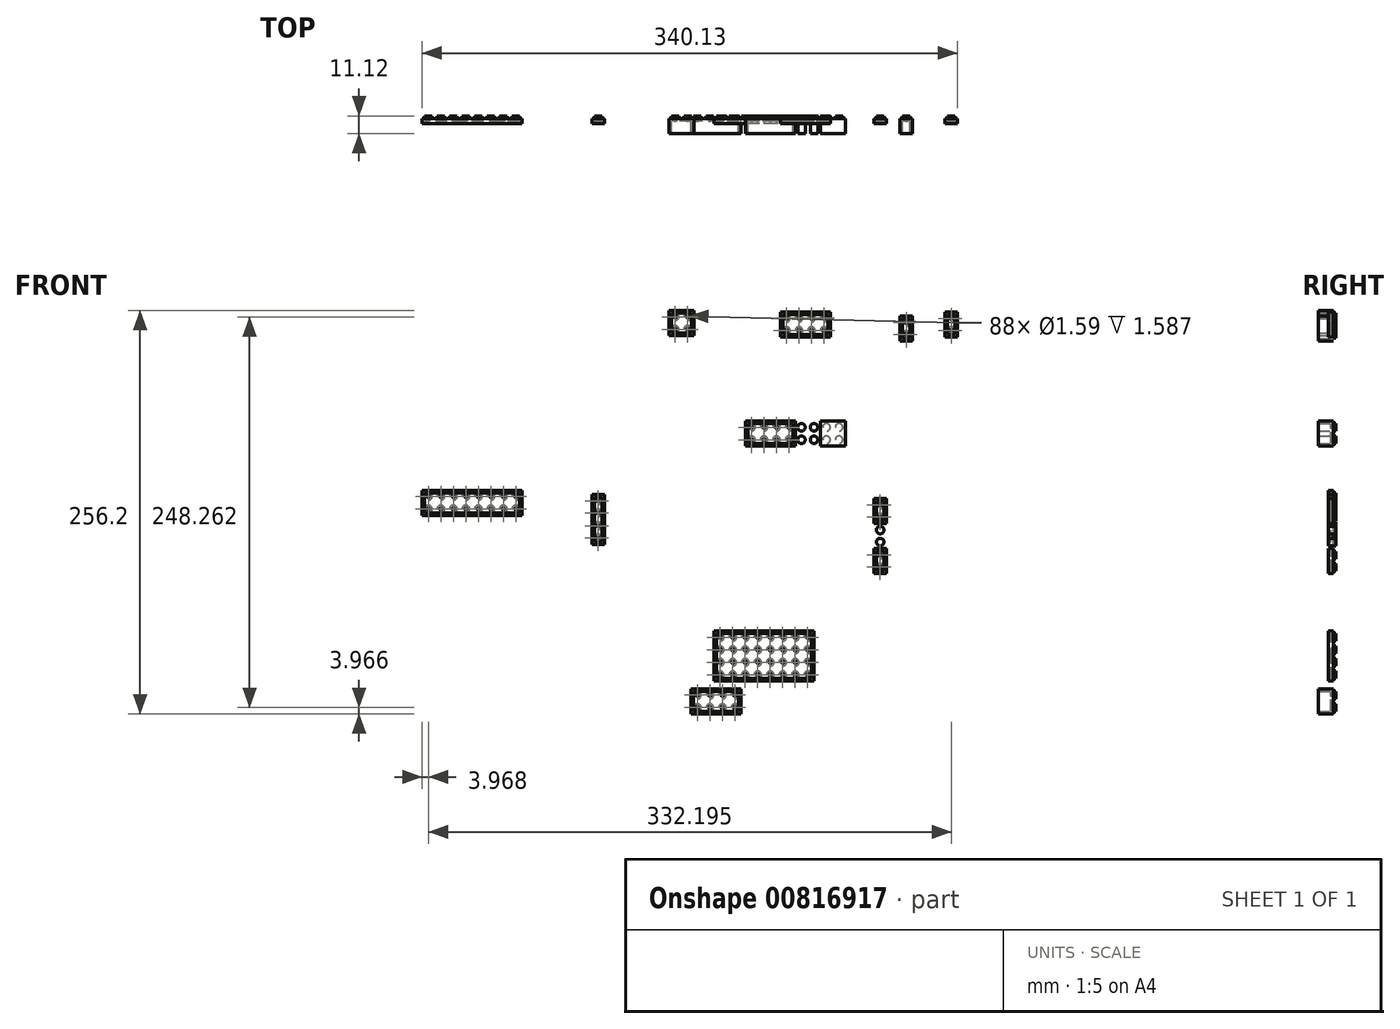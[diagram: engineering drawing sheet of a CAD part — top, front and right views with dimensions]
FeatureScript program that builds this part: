
annotation { "Feature Type Name" : "Feature", "Feature Type Description" : "" }
export const myFeature = defineFeature(function(context is Context, id is Id, definition is map)
    precondition{}
    {
        {
            var Q0;
            Q0=qCreatedBy(makeId("Front.planeOp"),FACE);
            var sketch = newSketch(context, id + "F0", { "sketchPlane" : qUnion([Q0])});
            skLineSegment(sketch, "E0.bottom", {"start": v(-97.11, 110.8) * mm, "end": v(-112.99, 110.8) * mm});
            skLineSegment(sketch, "E0.top", {"start": v(-97.11, 126.67) * mm, "end": v(-112.99, 126.67) * mm});
            skLineSegment(sketch, "E0.left", {"start": v(-97.11, 110.8) * mm, "end": v(-97.11, 126.67) * mm});
            skLineSegment(sketch, "E0.right", {"start": v(-112.99, 110.8) * mm, "end": v(-112.99, 126.67) * mm});
            skPoint(sketch, "E0.middle", {"position": v(-105.05, 118.73) * mm});
            skLineSegment(sketch, "E1", {"start": v(-97.11, 118.73) * mm, "end": v(-112.99, 118.73) * mm, "construction": true});
            skLineSegment(sketch, "E2", {"start": v(-105.05, 126.67) * mm, "end": v(-105.05, 110.8) * mm, "construction": true});
            skLineSegment(sketch, "E3.bottom", {"start": v(-101.08, 114.76) * mm, "end": v(-109.02, 114.76) * mm, "construction": true});
            skLineSegment(sketch, "E3.top", {"start": v(-101.08, 122.7) * mm, "end": v(-109.02, 122.7) * mm, "construction": true});
            skLineSegment(sketch, "E3.left", {"start": v(-101.08, 114.76) * mm, "end": v(-101.08, 122.7) * mm, "construction": true});
            skLineSegment(sketch, "E3.right", {"start": v(-109.02, 114.76) * mm, "end": v(-109.02, 122.7) * mm, "construction": true});
            skCircle(sketch, "E4", {"center": v(-109.02, 122.7) * mm, "radius": 2.38 * mm});
            skCircle(sketch, "E5", {"center": v(-101.08, 122.7) * mm, "radius": 2.38 * mm});
            skCircle(sketch, "E6", {"center": v(-101.08, 114.76) * mm, "radius": 2.38 * mm});
            skCircle(sketch, "E7", {"center": v(-109.02, 114.76) * mm, "radius": 2.38 * mm});
            skLineSegment(sketch, "E8.bottom", {"start": v(-26.35, 109.94) * mm, "end": v(-42.23, 109.94) * mm});
            skLineSegment(sketch, "E8.top", {"start": v(-26.35, 125.82) * mm, "end": v(-42.23, 125.82) * mm});
            skLineSegment(sketch, "E8.left", {"start": v(-26.35, 109.94) * mm, "end": v(-26.35, 125.82) * mm});
            skLineSegment(sketch, "E8.right", {"start": v(-42.23, 109.94) * mm, "end": v(-42.23, 125.82) * mm});
            skPoint(sketch, "E8.middle", {"position": v(-34.29, 117.88) * mm});
            skLineSegment(sketch, "E9", {"start": v(-26.35, 117.88) * mm, "end": v(-42.23, 117.88) * mm, "construction": true});
            skLineSegment(sketch, "E10", {"start": v(-34.29, 125.82) * mm, "end": v(-34.29, 109.94) * mm, "construction": true});
            skLineSegment(sketch, "E11.bottom", {"start": v(-30.32, 113.91) * mm, "end": v(-38.26, 113.91) * mm, "construction": true});
            skLineSegment(sketch, "E11.top", {"start": v(-30.32, 121.85) * mm, "end": v(-38.26, 121.85) * mm, "construction": true});
            skLineSegment(sketch, "E11.left", {"start": v(-30.32, 113.91) * mm, "end": v(-30.32, 121.85) * mm, "construction": true});
            skLineSegment(sketch, "E11.right", {"start": v(-38.26, 113.91) * mm, "end": v(-38.26, 121.85) * mm, "construction": true});
            skCircle(sketch, "E12", {"center": v(-38.26, 121.85) * mm, "radius": 2.38 * mm});
            skCircle(sketch, "E13", {"center": v(-30.32, 121.85) * mm, "radius": 2.38 * mm});
            skCircle(sketch, "E14", {"center": v(-30.32, 113.91) * mm, "radius": 2.38 * mm});
            skCircle(sketch, "E15", {"center": v(-38.26, 113.91) * mm, "radius": 2.38 * mm});
            skLineSegment(sketch, "E16.bottom", {"start": v(-10.48, 109.94) * mm, "end": v(-26.35, 109.94) * mm});
            skLineSegment(sketch, "E16.top", {"start": v(-10.48, 125.82) * mm, "end": v(-26.35, 125.82) * mm});
            skLineSegment(sketch, "E16.left", {"start": v(-10.48, 109.94) * mm, "end": v(-10.48, 125.82) * mm});
            skPoint(sketch, "E16.middle", {"position": v(-18.41, 117.88) * mm});
            skLineSegment(sketch, "E17", {"start": v(-10.48, 117.88) * mm, "end": v(-26.35, 117.88) * mm, "construction": true});
            skLineSegment(sketch, "E18", {"start": v(-18.41, 125.82) * mm, "end": v(-18.41, 109.94) * mm, "construction": true});
            skLineSegment(sketch, "E19.bottom", {"start": v(-14.44, 113.91) * mm, "end": v(-22.38, 113.91) * mm, "construction": true});
            skLineSegment(sketch, "E19.top", {"start": v(-14.44, 121.85) * mm, "end": v(-22.38, 121.85) * mm, "construction": true});
            skLineSegment(sketch, "E19.left", {"start": v(-14.44, 113.91) * mm, "end": v(-14.44, 121.85) * mm, "construction": true});
            skLineSegment(sketch, "E19.right", {"start": v(-22.38, 113.91) * mm, "end": v(-22.38, 121.85) * mm, "construction": true});
            skCircle(sketch, "E20", {"center": v(-22.38, 121.85) * mm, "radius": 2.38 * mm});
            skCircle(sketch, "E21", {"center": v(-14.44, 121.85) * mm, "radius": 2.38 * mm});
            skCircle(sketch, "E22", {"center": v(-14.44, 113.91) * mm, "radius": 2.38 * mm});
            skCircle(sketch, "E23", {"center": v(-22.38, 113.91) * mm, "radius": 2.38 * mm});
            skLineSegment(sketch, "E24.bottom", {"start": v(41.77, 107.4) * mm, "end": v(33.85, 107.4) * mm});
            skLineSegment(sketch, "E24.top", {"start": v(41.77, 123.28) * mm, "end": v(33.85, 123.28) * mm});
            skLineSegment(sketch, "E24.left", {"start": v(41.77, 107.4) * mm, "end": v(41.77, 123.28) * mm});
            skLineSegment(sketch, "E24.right", {"start": v(33.85, 107.4) * mm, "end": v(33.85, 123.28) * mm});
            skPoint(sketch, "E24.middle", {"position": v(37.8, 115.34) * mm});
            skLineSegment(sketch, "E25", {"start": v(37.8, 123.28) * mm, "end": v(37.8, 107.4) * mm, "construction": true});
            skLineSegment(sketch, "E26", {"start": v(33.85, 115.34) * mm, "end": v(41.77, 115.34) * mm, "construction": true});
            skLineSegment(sketch, "E27", {"start": v(33.85, 111.53) * mm, "end": v(41.77, 111.53) * mm, "construction": true});
            skLineSegment(sketch, "E28", {"start": v(33.85, 119.14) * mm, "end": v(41.77, 119.14) * mm, "construction": true});
            skCircle(sketch, "E29", {"center": v(37.8, 119.14) * mm, "radius": 2.38 * mm});
            skCircle(sketch, "E30", {"center": v(37.8, 111.53) * mm, "radius": 2.38 * mm});
            skLineSegment(sketch, "E31.bottom", {"start": v(-68.44, -92.83) * mm, "end": v(-84.32, -92.83) * mm});
            skLineSegment(sketch, "E31.top", {"start": v(-68.44, -76.96) * mm, "end": v(-84.32, -76.96) * mm});
            skLineSegment(sketch, "E31.left", {"start": v(-68.44, -92.83) * mm, "end": v(-68.44, -76.96) * mm});
            skLineSegment(sketch, "E31.right", {"start": v(-84.32, -92.83) * mm, "end": v(-84.32, -76.96) * mm});
            skPoint(sketch, "E31.middle", {"position": v(-76.38, -84.9) * mm});
            skLineSegment(sketch, "E32", {"start": v(-68.44, -84.9) * mm, "end": v(-84.32, -84.9) * mm, "construction": true});
            skLineSegment(sketch, "E33", {"start": v(-76.38, -76.96) * mm, "end": v(-76.38, -92.83) * mm, "construction": true});
            skLineSegment(sketch, "E34.bottom", {"start": v(-72.4, -88.86) * mm, "end": v(-80.35, -88.86) * mm, "construction": true});
            skLineSegment(sketch, "E34.top", {"start": v(-72.4, -80.93) * mm, "end": v(-80.35, -80.93) * mm, "construction": true});
            skLineSegment(sketch, "E34.left", {"start": v(-72.4, -88.86) * mm, "end": v(-72.4, -80.93) * mm, "construction": true});
            skLineSegment(sketch, "E34.right", {"start": v(-80.35, -88.86) * mm, "end": v(-80.35, -80.93) * mm, "construction": true});
            skCircle(sketch, "E35", {"center": v(-80.35, -80.93) * mm, "radius": 2.38 * mm});
            skCircle(sketch, "E36", {"center": v(-72.4, -80.93) * mm, "radius": 2.38 * mm});
            skCircle(sketch, "E37", {"center": v(-72.4, -88.86) * mm, "radius": 2.38 * mm});
            skCircle(sketch, "E38", {"center": v(-80.35, -88.86) * mm, "radius": 2.38 * mm});
            skLineSegment(sketch, "E39.bottom", {"start": v(-48.58, 40.58) * mm, "end": v(-64.45, 40.58) * mm});
            skLineSegment(sketch, "E39.top", {"start": v(-48.58, 56.46) * mm, "end": v(-64.45, 56.46) * mm});
            skLineSegment(sketch, "E39.left", {"start": v(-48.58, 40.58) * mm, "end": v(-48.58, 56.46) * mm});
            skLineSegment(sketch, "E39.right", {"start": v(-64.45, 40.58) * mm, "end": v(-64.45, 56.46) * mm});
            skPoint(sketch, "E39.middle", {"position": v(-56.51, 48.52) * mm});
            skLineSegment(sketch, "E40", {"start": v(-48.58, 48.52) * mm, "end": v(-64.45, 48.52) * mm, "construction": true});
            skLineSegment(sketch, "E41", {"start": v(-56.51, 56.46) * mm, "end": v(-56.51, 40.58) * mm, "construction": true});
            skLineSegment(sketch, "E42.bottom", {"start": v(-52.54, 44.55) * mm, "end": v(-60.48, 44.55) * mm, "construction": true});
            skLineSegment(sketch, "E42.top", {"start": v(-52.54, 52.49) * mm, "end": v(-60.48, 52.49) * mm, "construction": true});
            skLineSegment(sketch, "E42.left", {"start": v(-52.54, 44.55) * mm, "end": v(-52.54, 52.49) * mm, "construction": true});
            skLineSegment(sketch, "E42.right", {"start": v(-60.48, 44.55) * mm, "end": v(-60.48, 52.49) * mm, "construction": true});
            skCircle(sketch, "E43", {"center": v(-60.48, 52.49) * mm, "radius": 2.38 * mm});
            skCircle(sketch, "E44", {"center": v(-52.54, 52.49) * mm, "radius": 2.38 * mm});
            skCircle(sketch, "E45", {"center": v(-52.54, 44.55) * mm, "radius": 2.38 * mm});
            skCircle(sketch, "E46", {"center": v(-60.48, 44.55) * mm, "radius": 2.38 * mm});
            skLineSegment(sketch, "E47.bottom", {"start": v(-32.7, 40.58) * mm, "end": v(-48.58, 40.58) * mm});
            skLineSegment(sketch, "E47.top", {"start": v(-32.7, 56.46) * mm, "end": v(-48.58, 56.46) * mm});
            skLineSegment(sketch, "E47.left", {"start": v(-32.7, 40.58) * mm, "end": v(-32.7, 56.46) * mm});
            skPoint(sketch, "E47.middle", {"position": v(-40.64, 48.52) * mm});
            skLineSegment(sketch, "E48", {"start": v(-32.7, 48.52) * mm, "end": v(-48.58, 48.52) * mm, "construction": true});
            skLineSegment(sketch, "E49", {"start": v(-40.64, 56.46) * mm, "end": v(-40.64, 40.58) * mm, "construction": true});
            skLineSegment(sketch, "E50.bottom", {"start": v(-36.67, 44.55) * mm, "end": v(-44.6, 44.55) * mm, "construction": true});
            skLineSegment(sketch, "E50.top", {"start": v(-36.67, 52.49) * mm, "end": v(-44.6, 52.49) * mm, "construction": true});
            skLineSegment(sketch, "E50.left", {"start": v(-36.67, 44.55) * mm, "end": v(-36.67, 52.49) * mm, "construction": true});
            skLineSegment(sketch, "E50.right", {"start": v(-44.6, 44.55) * mm, "end": v(-44.6, 52.49) * mm, "construction": true});
            skCircle(sketch, "E51", {"center": v(-44.6, 52.49) * mm, "radius": 2.38 * mm});
            skCircle(sketch, "E52", {"center": v(-36.67, 52.49) * mm, "radius": 2.38 * mm});
            skCircle(sketch, "E53", {"center": v(-36.67, 44.55) * mm, "radius": 2.38 * mm});
            skCircle(sketch, "E54", {"center": v(-44.6, 44.55) * mm, "radius": 2.38 * mm});
            skLineSegment(sketch, "E55.bottom", {"start": v(70.44, 109.95) * mm, "end": v(62.51, 109.95) * mm});
            skLineSegment(sketch, "E55.top", {"start": v(70.44, 125.83) * mm, "end": v(62.51, 125.83) * mm});
            skLineSegment(sketch, "E55.left", {"start": v(70.44, 109.95) * mm, "end": v(70.44, 125.83) * mm});
            skLineSegment(sketch, "E55.right", {"start": v(62.51, 109.95) * mm, "end": v(62.51, 125.83) * mm});
            skPoint(sketch, "E55.middle", {"position": v(66.47, 117.89) * mm});
            skLineSegment(sketch, "E56", {"start": v(66.47, 125.83) * mm, "end": v(66.47, 109.95) * mm, "construction": true});
            skLineSegment(sketch, "E57", {"start": v(62.51, 117.89) * mm, "end": v(70.44, 117.89) * mm, "construction": true});
            skLineSegment(sketch, "E58", {"start": v(62.51, 114.08) * mm, "end": v(70.44, 114.08) * mm, "construction": true});
            skLineSegment(sketch, "E59", {"start": v(62.51, 121.69) * mm, "end": v(70.44, 121.69) * mm, "construction": true});
            skCircle(sketch, "E60", {"center": v(66.47, 121.69) * mm, "radius": 2.38 * mm});
            skCircle(sketch, "E61", {"center": v(66.47, 114.08) * mm, "radius": 2.38 * mm});
            skLineSegment(sketch, "E62.bottom", {"start": v(-52.57, -92.83) * mm, "end": v(-68.44, -92.83) * mm});
            skLineSegment(sketch, "E62.top", {"start": v(-52.57, -76.96) * mm, "end": v(-68.44, -76.96) * mm});
            skLineSegment(sketch, "E62.left", {"start": v(-52.57, -92.83) * mm, "end": v(-52.57, -76.96) * mm});
            skPoint(sketch, "E62.middle", {"position": v(-60.5, -84.9) * mm});
            skLineSegment(sketch, "E63", {"start": v(-52.57, -84.9) * mm, "end": v(-68.44, -84.9) * mm, "construction": true});
            skLineSegment(sketch, "E64", {"start": v(-60.5, -76.96) * mm, "end": v(-60.5, -92.83) * mm, "construction": true});
            skLineSegment(sketch, "E65.bottom", {"start": v(-56.53, -88.86) * mm, "end": v(-64.47, -88.86) * mm, "construction": true});
            skLineSegment(sketch, "E65.top", {"start": v(-56.53, -80.93) * mm, "end": v(-64.47, -80.93) * mm, "construction": true});
            skLineSegment(sketch, "E65.left", {"start": v(-56.53, -88.86) * mm, "end": v(-56.53, -80.93) * mm, "construction": true});
            skLineSegment(sketch, "E65.right", {"start": v(-64.47, -88.86) * mm, "end": v(-64.47, -80.93) * mm, "construction": true});
            skCircle(sketch, "E66", {"center": v(-64.47, -80.93) * mm, "radius": 2.38 * mm});
            skCircle(sketch, "E67", {"center": v(-56.53, -80.93) * mm, "radius": 2.38 * mm});
            skCircle(sketch, "E68", {"center": v(-56.53, -88.86) * mm, "radius": 2.38 * mm});
            skCircle(sketch, "E69", {"center": v(-64.47, -88.86) * mm, "radius": 2.38 * mm});
            skLineSegment(sketch, "E70.bottom", {"start": v(-36.7, -92.83) * mm, "end": v(-52.57, -92.83) * mm});
            skLineSegment(sketch, "E70.top", {"start": v(-36.7, -76.96) * mm, "end": v(-52.57, -76.96) * mm});
            skLineSegment(sketch, "E70.left", {"start": v(-36.7, -92.83) * mm, "end": v(-36.7, -76.96) * mm});
            skPoint(sketch, "E70.middle", {"position": v(-44.63, -84.9) * mm});
            skLineSegment(sketch, "E71", {"start": v(-36.7, -84.9) * mm, "end": v(-52.57, -84.9) * mm, "construction": true});
            skLineSegment(sketch, "E72", {"start": v(-44.63, -76.96) * mm, "end": v(-44.63, -92.83) * mm, "construction": true});
            skLineSegment(sketch, "E73.bottom", {"start": v(-40.66, -88.86) * mm, "end": v(-48.6, -88.86) * mm, "construction": true});
            skLineSegment(sketch, "E73.top", {"start": v(-40.66, -80.93) * mm, "end": v(-48.6, -80.93) * mm, "construction": true});
            skLineSegment(sketch, "E73.left", {"start": v(-40.66, -88.86) * mm, "end": v(-40.66, -80.93) * mm, "construction": true});
            skLineSegment(sketch, "E73.right", {"start": v(-48.6, -88.86) * mm, "end": v(-48.6, -80.93) * mm, "construction": true});
            skCircle(sketch, "E74", {"center": v(-48.6, -80.93) * mm, "radius": 2.38 * mm});
            skCircle(sketch, "E75", {"center": v(-40.66, -80.93) * mm, "radius": 2.38 * mm});
            skCircle(sketch, "E76", {"center": v(-40.66, -88.86) * mm, "radius": 2.38 * mm});
            skCircle(sketch, "E77", {"center": v(-48.6, -88.86) * mm, "radius": 2.38 * mm});
            skLineSegment(sketch, "E78.bottom", {"start": v(-20.82, -92.83) * mm, "end": v(-36.7, -92.83) * mm});
            skLineSegment(sketch, "E78.top", {"start": v(-20.82, -76.96) * mm, "end": v(-36.7, -76.96) * mm});
            skLineSegment(sketch, "E78.left", {"start": v(-20.82, -92.83) * mm, "end": v(-20.82, -76.96) * mm});
            skPoint(sketch, "E78.middle", {"position": v(-28.75, -84.9) * mm});
            skLineSegment(sketch, "E79", {"start": v(-20.82, -84.9) * mm, "end": v(-36.7, -84.9) * mm, "construction": true});
            skLineSegment(sketch, "E80", {"start": v(-28.75, -76.96) * mm, "end": v(-28.75, -92.83) * mm, "construction": true});
            skLineSegment(sketch, "E81.bottom", {"start": v(-24.78, -88.86) * mm, "end": v(-32.72, -88.86) * mm, "construction": true});
            skLineSegment(sketch, "E81.top", {"start": v(-24.78, -80.93) * mm, "end": v(-32.72, -80.93) * mm, "construction": true});
            skLineSegment(sketch, "E81.left", {"start": v(-24.78, -88.86) * mm, "end": v(-24.78, -80.93) * mm, "construction": true});
            skLineSegment(sketch, "E81.right", {"start": v(-32.72, -88.86) * mm, "end": v(-32.72, -80.93) * mm, "construction": true});
            skCircle(sketch, "E82", {"center": v(-32.72, -80.93) * mm, "radius": 2.38 * mm});
            skCircle(sketch, "E83", {"center": v(-24.78, -80.93) * mm, "radius": 2.38 * mm});
            skCircle(sketch, "E84", {"center": v(-24.78, -88.86) * mm, "radius": 2.38 * mm});
            skCircle(sketch, "E85", {"center": v(-32.72, -88.86) * mm, "radius": 2.38 * mm});
            skLineSegment(sketch, "E86.bottom", {"start": v(25.2, -8.63) * mm, "end": v(17.27, -8.63) * mm});
            skLineSegment(sketch, "E86.top", {"start": v(25.2, 7.25) * mm, "end": v(17.27, 7.25) * mm});
            skLineSegment(sketch, "E86.left", {"start": v(25.2, -8.63) * mm, "end": v(25.2, 7.25) * mm});
            skLineSegment(sketch, "E86.right", {"start": v(17.27, -8.63) * mm, "end": v(17.27, 7.25) * mm});
            skPoint(sketch, "E86.middle", {"position": v(21.23, -0.69) * mm});
            skLineSegment(sketch, "E87", {"start": v(21.23, 7.25) * mm, "end": v(21.23, -8.63) * mm, "construction": true});
            skLineSegment(sketch, "E88", {"start": v(17.27, -0.69) * mm, "end": v(25.2, -0.69) * mm, "construction": true});
            skLineSegment(sketch, "E89", {"start": v(17.27, -4.5) * mm, "end": v(25.2, -4.5) * mm, "construction": true});
            skLineSegment(sketch, "E90", {"start": v(17.27, 3.1) * mm, "end": v(25.2, 3.1) * mm, "construction": true});
            skCircle(sketch, "E91", {"center": v(21.23, 3.1) * mm, "radius": 2.38 * mm});
            skCircle(sketch, "E92", {"center": v(21.23, -4.5) * mm, "radius": 2.38 * mm});
            skLineSegment(sketch, "E93.bottom", {"start": v(-68.44, -108.7) * mm, "end": v(-84.32, -108.7) * mm});
            skLineSegment(sketch, "E93.left", {"start": v(-68.44, -108.7) * mm, "end": v(-68.44, -92.83) * mm});
            skLineSegment(sketch, "E93.right", {"start": v(-84.32, -108.7) * mm, "end": v(-84.32, -92.83) * mm});
            skPoint(sketch, "E93.middle", {"position": v(-76.38, -100.77) * mm});
            skLineSegment(sketch, "E94", {"start": v(-68.44, -100.77) * mm, "end": v(-84.32, -100.77) * mm, "construction": true});
            skLineSegment(sketch, "E95", {"start": v(-76.38, -92.83) * mm, "end": v(-76.38, -108.7) * mm, "construction": true});
            skLineSegment(sketch, "E96.bottom", {"start": v(-72.4, -104.74) * mm, "end": v(-80.35, -104.74) * mm, "construction": true});
            skLineSegment(sketch, "E96.top", {"start": v(-72.4, -96.8) * mm, "end": v(-80.35, -96.8) * mm, "construction": true});
            skLineSegment(sketch, "E96.left", {"start": v(-72.4, -104.74) * mm, "end": v(-72.4, -96.8) * mm, "construction": true});
            skLineSegment(sketch, "E96.right", {"start": v(-80.35, -104.74) * mm, "end": v(-80.35, -96.8) * mm, "construction": true});
            skCircle(sketch, "E97", {"center": v(-80.35, -96.8) * mm, "radius": 2.38 * mm});
            skCircle(sketch, "E98", {"center": v(-72.4, -96.8) * mm, "radius": 2.38 * mm});
            skCircle(sketch, "E99", {"center": v(-72.4, -104.74) * mm, "radius": 2.38 * mm});
            skCircle(sketch, "E100", {"center": v(-80.35, -104.74) * mm, "radius": 2.38 * mm});
            skLineSegment(sketch, "E101.bottom", {"start": v(-82.95, -129.53) * mm, "end": v(-98.82, -129.53) * mm});
            skLineSegment(sketch, "E101.top", {"start": v(-82.95, -113.66) * mm, "end": v(-98.82, -113.66) * mm});
            skLineSegment(sketch, "E101.left", {"start": v(-82.95, -129.53) * mm, "end": v(-82.95, -113.66) * mm});
            skLineSegment(sketch, "E101.right", {"start": v(-98.82, -129.53) * mm, "end": v(-98.82, -113.66) * mm});
            skPoint(sketch, "E101.middle", {"position": v(-90.89, -121.6) * mm});
            skLineSegment(sketch, "E102", {"start": v(-82.95, -121.6) * mm, "end": v(-98.82, -121.6) * mm, "construction": true});
            skLineSegment(sketch, "E103", {"start": v(-90.89, -113.66) * mm, "end": v(-90.89, -129.53) * mm, "construction": true});
            skLineSegment(sketch, "E104.bottom", {"start": v(-86.92, -125.56) * mm, "end": v(-94.85, -125.56) * mm, "construction": true});
            skLineSegment(sketch, "E104.top", {"start": v(-86.92, -117.63) * mm, "end": v(-94.85, -117.63) * mm, "construction": true});
            skLineSegment(sketch, "E104.left", {"start": v(-86.92, -125.56) * mm, "end": v(-86.92, -117.63) * mm, "construction": true});
            skLineSegment(sketch, "E104.right", {"start": v(-94.85, -125.56) * mm, "end": v(-94.85, -117.63) * mm, "construction": true});
            skCircle(sketch, "E105", {"center": v(-94.85, -117.63) * mm, "radius": 2.38 * mm});
            skCircle(sketch, "E106", {"center": v(-86.92, -117.63) * mm, "radius": 2.38 * mm});
            skCircle(sketch, "E107", {"center": v(-86.92, -125.56) * mm, "radius": 2.38 * mm});
            skCircle(sketch, "E108", {"center": v(-94.85, -125.56) * mm, "radius": 2.38 * mm});
            skLineSegment(sketch, "E109.bottom", {"start": v(-67.07, -129.53) * mm, "end": v(-82.95, -129.53) * mm});
            skLineSegment(sketch, "E109.top", {"start": v(-67.07, -113.66) * mm, "end": v(-82.95, -113.66) * mm});
            skLineSegment(sketch, "E109.left", {"start": v(-67.07, -129.53) * mm, "end": v(-67.07, -113.66) * mm});
            skPoint(sketch, "E109.middle", {"position": v(-75.01, -121.6) * mm});
            skLineSegment(sketch, "E110", {"start": v(-67.07, -121.6) * mm, "end": v(-82.95, -121.6) * mm, "construction": true});
            skLineSegment(sketch, "E111", {"start": v(-75.01, -113.66) * mm, "end": v(-75.01, -129.53) * mm, "construction": true});
            skLineSegment(sketch, "E112.bottom", {"start": v(-71.04, -125.56) * mm, "end": v(-78.98, -125.56) * mm, "construction": true});
            skLineSegment(sketch, "E112.top", {"start": v(-71.04, -117.63) * mm, "end": v(-78.98, -117.63) * mm, "construction": true});
            skLineSegment(sketch, "E112.left", {"start": v(-71.04, -125.56) * mm, "end": v(-71.04, -117.63) * mm, "construction": true});
            skLineSegment(sketch, "E112.right", {"start": v(-78.98, -125.56) * mm, "end": v(-78.98, -117.63) * mm, "construction": true});
            skCircle(sketch, "E113", {"center": v(-78.98, -117.63) * mm, "radius": 2.38 * mm});
            skCircle(sketch, "E114", {"center": v(-71.04, -117.63) * mm, "radius": 2.38 * mm});
            skCircle(sketch, "E115", {"center": v(-71.04, -125.56) * mm, "radius": 2.38 * mm});
            skCircle(sketch, "E116", {"center": v(-78.98, -125.56) * mm, "radius": 2.38 * mm});
            skLineSegment(sketch, "E117.bottom", {"start": v(25.2, -40.38) * mm, "end": v(17.27, -40.38) * mm});
            skLineSegment(sketch, "E117.top", {"start": v(25.2, -24.5) * mm, "end": v(17.27, -24.5) * mm});
            skLineSegment(sketch, "E117.left", {"start": v(25.2, -40.38) * mm, "end": v(25.2, -24.5) * mm});
            skLineSegment(sketch, "E117.right", {"start": v(17.27, -40.38) * mm, "end": v(17.27, -24.5) * mm});
            skPoint(sketch, "E117.middle", {"position": v(21.23, -32.44) * mm});
            skLineSegment(sketch, "E118", {"start": v(21.23, -24.5) * mm, "end": v(21.23, -40.38) * mm, "construction": true});
            skLineSegment(sketch, "E119", {"start": v(17.27, -32.44) * mm, "end": v(25.2, -32.44) * mm, "construction": true});
            skLineSegment(sketch, "E120", {"start": v(17.27, -36.25) * mm, "end": v(25.2, -36.25) * mm, "construction": true});
            skLineSegment(sketch, "E121", {"start": v(17.27, -28.64) * mm, "end": v(25.2, -28.64) * mm, "construction": true});
            skCircle(sketch, "E122", {"center": v(21.23, -28.64) * mm, "radius": 2.38 * mm});
            skCircle(sketch, "E123", {"center": v(21.23, -36.25) * mm, "radius": 2.38 * mm});
            skLineSegment(sketch, "E124.bottom", {"start": v(-52.57, -108.7) * mm, "end": v(-68.44, -108.7) * mm});
            skLineSegment(sketch, "E124.left", {"start": v(-52.57, -108.7) * mm, "end": v(-52.57, -92.83) * mm});
            skPoint(sketch, "E124.middle", {"position": v(-60.5, -100.77) * mm});
            skLineSegment(sketch, "E125", {"start": v(-52.57, -100.77) * mm, "end": v(-68.44, -100.77) * mm, "construction": true});
            skLineSegment(sketch, "E126", {"start": v(-60.5, -92.83) * mm, "end": v(-60.5, -108.7) * mm, "construction": true});
            skLineSegment(sketch, "E127.bottom", {"start": v(-56.53, -104.74) * mm, "end": v(-64.47, -104.74) * mm, "construction": true});
            skLineSegment(sketch, "E127.top", {"start": v(-56.53, -96.8) * mm, "end": v(-64.47, -96.8) * mm, "construction": true});
            skLineSegment(sketch, "E127.left", {"start": v(-56.53, -104.74) * mm, "end": v(-56.53, -96.8) * mm, "construction": true});
            skLineSegment(sketch, "E127.right", {"start": v(-64.47, -104.74) * mm, "end": v(-64.47, -96.8) * mm, "construction": true});
            skCircle(sketch, "E128", {"center": v(-64.47, -96.8) * mm, "radius": 2.38 * mm});
            skCircle(sketch, "E129", {"center": v(-56.53, -96.8) * mm, "radius": 2.38 * mm});
            skCircle(sketch, "E130", {"center": v(-56.53, -104.74) * mm, "radius": 2.38 * mm});
            skCircle(sketch, "E131", {"center": v(-64.47, -104.74) * mm, "radius": 2.38 * mm});
            skLineSegment(sketch, "E132.bottom", {"start": v(-36.7, -108.7) * mm, "end": v(-52.57, -108.7) * mm});
            skLineSegment(sketch, "E132.left", {"start": v(-36.7, -108.7) * mm, "end": v(-36.7, -92.83) * mm});
            skPoint(sketch, "E132.middle", {"position": v(-44.63, -100.77) * mm});
            skLineSegment(sketch, "E133", {"start": v(-36.7, -100.77) * mm, "end": v(-52.57, -100.77) * mm, "construction": true});
            skLineSegment(sketch, "E134", {"start": v(-44.63, -92.83) * mm, "end": v(-44.63, -108.7) * mm, "construction": true});
            skLineSegment(sketch, "E135.bottom", {"start": v(-40.66, -104.74) * mm, "end": v(-48.6, -104.74) * mm, "construction": true});
            skLineSegment(sketch, "E135.top", {"start": v(-40.66, -96.8) * mm, "end": v(-48.6, -96.8) * mm, "construction": true});
            skLineSegment(sketch, "E135.left", {"start": v(-40.66, -104.74) * mm, "end": v(-40.66, -96.8) * mm, "construction": true});
            skLineSegment(sketch, "E135.right", {"start": v(-48.6, -104.74) * mm, "end": v(-48.6, -96.8) * mm, "construction": true});
            skCircle(sketch, "E136", {"center": v(-48.6, -96.8) * mm, "radius": 2.38 * mm});
            skCircle(sketch, "E137", {"center": v(-40.66, -96.8) * mm, "radius": 2.38 * mm});
            skCircle(sketch, "E138", {"center": v(-40.66, -104.74) * mm, "radius": 2.38 * mm});
            skCircle(sketch, "E139", {"center": v(-48.6, -104.74) * mm, "radius": 2.38 * mm});
            skLineSegment(sketch, "E140.bottom", {"start": v(-20.82, -108.7) * mm, "end": v(-36.7, -108.7) * mm});
            skLineSegment(sketch, "E140.left", {"start": v(-20.82, -108.7) * mm, "end": v(-20.82, -92.83) * mm});
            skPoint(sketch, "E140.middle", {"position": v(-28.75, -100.77) * mm});
            skLineSegment(sketch, "E141", {"start": v(-20.82, -100.77) * mm, "end": v(-36.7, -100.77) * mm, "construction": true});
            skLineSegment(sketch, "E142", {"start": v(-28.75, -92.83) * mm, "end": v(-28.75, -108.7) * mm, "construction": true});
            skLineSegment(sketch, "E143.bottom", {"start": v(-24.78, -104.74) * mm, "end": v(-32.72, -104.74) * mm, "construction": true});
            skLineSegment(sketch, "E143.top", {"start": v(-24.78, -96.8) * mm, "end": v(-32.72, -96.8) * mm, "construction": true});
            skLineSegment(sketch, "E143.left", {"start": v(-24.78, -104.74) * mm, "end": v(-24.78, -96.8) * mm, "construction": true});
            skLineSegment(sketch, "E143.right", {"start": v(-32.72, -104.74) * mm, "end": v(-32.72, -96.8) * mm, "construction": true});
            skCircle(sketch, "E144", {"center": v(-32.72, -96.8) * mm, "radius": 2.38 * mm});
            skCircle(sketch, "E145", {"center": v(-24.78, -96.8) * mm, "radius": 2.38 * mm});
            skCircle(sketch, "E146", {"center": v(-24.78, -104.74) * mm, "radius": 2.38 * mm});
            skCircle(sketch, "E147", {"center": v(-32.72, -104.74) * mm, "radius": 2.38 * mm});
            skLineSegment(sketch, "E148.left", {"start": v(25.2, -24.5) * mm, "end": v(25.2, -8.63) * mm});
            skLineSegment(sketch, "E148.right", {"start": v(17.27, -24.5) * mm, "end": v(17.27, -8.63) * mm});
            skPoint(sketch, "E148.middle", {"position": v(21.23, -16.56) * mm});
            skLineSegment(sketch, "E149", {"start": v(21.23, -8.63) * mm, "end": v(21.23, -24.5) * mm, "construction": true});
            skLineSegment(sketch, "E150", {"start": v(17.27, -16.56) * mm, "end": v(25.2, -16.56) * mm, "construction": true});
            skLineSegment(sketch, "E151", {"start": v(17.27, -20.37) * mm, "end": v(25.2, -20.37) * mm, "construction": true});
            skLineSegment(sketch, "E152", {"start": v(17.27, -12.77) * mm, "end": v(25.2, -12.77) * mm, "construction": true});
            skCircle(sketch, "E153", {"center": v(21.23, -12.77) * mm, "radius": 2.38 * mm});
            skCircle(sketch, "E154", {"center": v(21.23, -20.37) * mm, "radius": 2.38 * mm});
            skLineSegment(sketch, "E155.bottom", {"start": v(-32.7, 40.58) * mm, "end": v(-0.95, 40.58) * mm});
            skLineSegment(sketch, "E155.top", {"start": v(-32.7, 56.46) * mm, "end": v(-0.95, 56.46) * mm});
            skLineSegment(sketch, "E155.right", {"start": v(-0.95, 40.58) * mm, "end": v(-0.95, 56.46) * mm});
            skLineSegment(sketch, "E156", {"start": v(-16.83, 56.46) * mm, "end": v(-16.83, 40.58) * mm});
            skLineSegment(sketch, "E157", {"start": v(-32.7, 48.52) * mm, "end": v(-0.95, 48.52) * mm, "construction": true});
            skLineSegment(sketch, "E158", {"start": v(-24.76, 40.58) * mm, "end": v(-24.76, 56.46) * mm, "construction": true});
            skLineSegment(sketch, "E159", {"start": v(-8.89, 40.58) * mm, "end": v(-8.89, 56.46) * mm, "construction": true});
            skLineSegment(sketch, "E160.bottom", {"start": v(-20.8, 44.55) * mm, "end": v(-28.73, 44.55) * mm, "construction": true});
            skLineSegment(sketch, "E160.top", {"start": v(-20.8, 52.49) * mm, "end": v(-28.73, 52.49) * mm, "construction": true});
            skLineSegment(sketch, "E160.left", {"start": v(-20.8, 44.55) * mm, "end": v(-20.8, 52.49) * mm, "construction": true});
            skLineSegment(sketch, "E160.right", {"start": v(-28.73, 44.55) * mm, "end": v(-28.73, 52.49) * mm, "construction": true});
            skPoint(sketch, "E160.middle", {"position": v(-24.76, 48.52) * mm});
            skLineSegment(sketch, "E161.bottom", {"start": v(-12.86, 44.55) * mm, "end": v(-4.92, 44.55) * mm, "construction": true});
            skLineSegment(sketch, "E161.top", {"start": v(-12.86, 52.49) * mm, "end": v(-4.92, 52.49) * mm, "construction": true});
            skLineSegment(sketch, "E161.left", {"start": v(-12.86, 44.55) * mm, "end": v(-12.86, 52.49) * mm, "construction": true});
            skLineSegment(sketch, "E161.right", {"start": v(-4.92, 44.55) * mm, "end": v(-4.92, 52.49) * mm, "construction": true});
            skPoint(sketch, "E161.middle", {"position": v(-8.89, 48.52) * mm});
            skCircle(sketch, "E162", {"center": v(-28.73, 52.49) * mm, "radius": 2.38 * mm});
            skCircle(sketch, "E163", {"center": v(-20.8, 52.49) * mm, "radius": 2.38 * mm});
            skCircle(sketch, "E164", {"center": v(-20.8, 44.55) * mm, "radius": 2.38 * mm});
            skCircle(sketch, "E165", {"center": v(-28.73, 44.55) * mm, "radius": 2.38 * mm});
            skCircle(sketch, "E166", {"center": v(-12.86, 44.55) * mm, "radius": 2.38 * mm});
            skCircle(sketch, "E167", {"center": v(-4.92, 44.55) * mm, "radius": 2.38 * mm});
            skCircle(sketch, "E168", {"center": v(-4.92, 52.49) * mm, "radius": 2.38 * mm});
            skCircle(sketch, "E169", {"center": v(-12.86, 52.49) * mm, "radius": 2.38 * mm});
            skLineSegment(sketch, "E170.bottom", {"start": v(-330.16, -43.54) * mm, "end": v(-346.04, -43.54) * mm});
            skLineSegment(sketch, "E170.top", {"start": v(-330.16, -27.67) * mm, "end": v(-346.04, -27.67) * mm});
            skLineSegment(sketch, "E170.left", {"start": v(-330.16, -43.54) * mm, "end": v(-330.16, -27.67) * mm});
            skLineSegment(sketch, "E170.right", {"start": v(-346.04, -43.54) * mm, "end": v(-346.04, -27.67) * mm});
            skPoint(sketch, "E170.middle", {"position": v(-338.1, -35.6) * mm});
            skLineSegment(sketch, "E171", {"start": v(-330.16, -35.6) * mm, "end": v(-346.04, -35.6) * mm, "construction": true});
            skLineSegment(sketch, "E172", {"start": v(-338.1, -27.67) * mm, "end": v(-338.1, -43.54) * mm, "construction": true});
            skLineSegment(sketch, "E173.bottom", {"start": v(-334.13, -39.57) * mm, "end": v(-342.07, -39.57) * mm, "construction": true});
            skLineSegment(sketch, "E173.top", {"start": v(-334.13, -31.63) * mm, "end": v(-342.07, -31.63) * mm, "construction": true});
            skLineSegment(sketch, "E173.left", {"start": v(-334.13, -39.57) * mm, "end": v(-334.13, -31.63) * mm, "construction": true});
            skLineSegment(sketch, "E173.right", {"start": v(-342.07, -39.57) * mm, "end": v(-342.07, -31.63) * mm, "construction": true});
            skCircle(sketch, "E174", {"center": v(-342.07, -31.63) * mm, "radius": 2.38 * mm});
            skCircle(sketch, "E175", {"center": v(-334.13, -31.63) * mm, "radius": 2.38 * mm});
            skCircle(sketch, "E176", {"center": v(-334.13, -39.57) * mm, "radius": 2.38 * mm});
            skCircle(sketch, "E177", {"center": v(-342.07, -39.57) * mm, "radius": 2.38 * mm});
            skLineSegment(sketch, "E178.bottom", {"start": v(-222.07, -3.36) * mm, "end": v(-237.94, -3.36) * mm});
            skLineSegment(sketch, "E178.top", {"start": v(-222.07, 12.51) * mm, "end": v(-237.94, 12.51) * mm});
            skLineSegment(sketch, "E178.left", {"start": v(-222.07, -3.36) * mm, "end": v(-222.07, 12.51) * mm});
            skLineSegment(sketch, "E178.right", {"start": v(-237.94, -3.36) * mm, "end": v(-237.94, 12.51) * mm});
            skPoint(sketch, "E178.middle", {"position": v(-230, 4.58) * mm});
            skLineSegment(sketch, "E179", {"start": v(-222.07, 4.58) * mm, "end": v(-237.94, 4.58) * mm, "construction": true});
            skLineSegment(sketch, "E180", {"start": v(-230, 12.51) * mm, "end": v(-230, -3.36) * mm, "construction": true});
            skLineSegment(sketch, "E181.bottom", {"start": v(-226.03, 0.6) * mm, "end": v(-233.97, 0.6) * mm, "construction": true});
            skLineSegment(sketch, "E181.top", {"start": v(-226.03, 8.54) * mm, "end": v(-233.97, 8.54) * mm, "construction": true});
            skLineSegment(sketch, "E181.left", {"start": v(-226.03, 0.6) * mm, "end": v(-226.03, 8.54) * mm, "construction": true});
            skLineSegment(sketch, "E181.right", {"start": v(-233.97, 0.6) * mm, "end": v(-233.97, 8.54) * mm, "construction": true});
            skCircle(sketch, "E182", {"center": v(-233.97, 8.54) * mm, "radius": 2.38 * mm});
            skCircle(sketch, "E183", {"center": v(-226.03, 8.54) * mm, "radius": 2.38 * mm});
            skCircle(sketch, "E184", {"center": v(-226.03, 0.6) * mm, "radius": 2.38 * mm});
            skCircle(sketch, "E185", {"center": v(-233.97, 0.6) * mm, "radius": 2.38 * mm});
            skLineSegment(sketch, "E186.bottom", {"start": v(-206.2, -3.36) * mm, "end": v(-222.07, -3.36) * mm});
            skLineSegment(sketch, "E186.top", {"start": v(-206.2, 12.51) * mm, "end": v(-222.07, 12.51) * mm});
            skLineSegment(sketch, "E186.left", {"start": v(-206.2, -3.36) * mm, "end": v(-206.2, 12.51) * mm});
            skPoint(sketch, "E186.middle", {"position": v(-214.13, 4.58) * mm});
            skLineSegment(sketch, "E187", {"start": v(-206.2, 4.58) * mm, "end": v(-222.07, 4.58) * mm, "construction": true});
            skLineSegment(sketch, "E188", {"start": v(-214.13, 12.51) * mm, "end": v(-214.13, -3.36) * mm, "construction": true});
            skLineSegment(sketch, "E189.bottom", {"start": v(-210.16, 0.6) * mm, "end": v(-218.1, 0.6) * mm, "construction": true});
            skLineSegment(sketch, "E189.top", {"start": v(-210.16, 8.54) * mm, "end": v(-218.1, 8.54) * mm, "construction": true});
            skLineSegment(sketch, "E189.left", {"start": v(-210.16, 0.6) * mm, "end": v(-210.16, 8.54) * mm, "construction": true});
            skLineSegment(sketch, "E189.right", {"start": v(-218.1, 0.6) * mm, "end": v(-218.1, 8.54) * mm, "construction": true});
            skCircle(sketch, "E190", {"center": v(-218.1, 8.54) * mm, "radius": 2.38 * mm});
            skCircle(sketch, "E191", {"center": v(-210.16, 8.54) * mm, "radius": 2.38 * mm});
            skCircle(sketch, "E192", {"center": v(-210.16, 0.6) * mm, "radius": 2.38 * mm});
            skCircle(sketch, "E193", {"center": v(-218.1, 0.6) * mm, "radius": 2.38 * mm});
            skLineSegment(sketch, "E194.bottom", {"start": v(-154, -5.9) * mm, "end": v(-161.92, -5.9) * mm});
            skLineSegment(sketch, "E194.top", {"start": v(-154, 9.97) * mm, "end": v(-161.92, 9.97) * mm});
            skLineSegment(sketch, "E194.left", {"start": v(-154, -5.9) * mm, "end": v(-154, 9.97) * mm});
            skLineSegment(sketch, "E194.right", {"start": v(-161.92, -5.9) * mm, "end": v(-161.92, 9.97) * mm});
            skPoint(sketch, "E194.middle", {"position": v(-157.96, 2.04) * mm});
            skLineSegment(sketch, "E195", {"start": v(-157.96, 9.97) * mm, "end": v(-157.96, -5.9) * mm, "construction": true});
            skLineSegment(sketch, "E196", {"start": v(-161.92, 2.04) * mm, "end": v(-154, 2.04) * mm, "construction": true});
            skLineSegment(sketch, "E197", {"start": v(-161.92, -1.77) * mm, "end": v(-154, -1.77) * mm, "construction": true});
            skLineSegment(sketch, "E198", {"start": v(-161.92, 5.83) * mm, "end": v(-154, 5.83) * mm, "construction": true});
            skCircle(sketch, "E199", {"center": v(-157.96, 5.83) * mm, "radius": 2.38 * mm});
            skCircle(sketch, "E200", {"center": v(-157.96, -1.77) * mm, "radius": 2.38 * mm});
            skLineSegment(sketch, "E201.bottom", {"start": v(-275.92, -106.34) * mm, "end": v(-291.8, -106.34) * mm});
            skLineSegment(sketch, "E201.top", {"start": v(-275.92, -90.47) * mm, "end": v(-291.8, -90.47) * mm});
            skLineSegment(sketch, "E201.left", {"start": v(-275.92, -106.34) * mm, "end": v(-275.92, -90.47) * mm});
            skLineSegment(sketch, "E201.right", {"start": v(-291.8, -106.34) * mm, "end": v(-291.8, -90.47) * mm});
            skPoint(sketch, "E201.middle", {"position": v(-283.86, -98.4) * mm});
            skLineSegment(sketch, "E202", {"start": v(-275.92, -98.4) * mm, "end": v(-291.8, -98.4) * mm, "construction": true});
            skLineSegment(sketch, "E203", {"start": v(-283.86, -90.47) * mm, "end": v(-283.86, -106.34) * mm, "construction": true});
            skLineSegment(sketch, "E204.bottom", {"start": v(-279.89, -102.37) * mm, "end": v(-287.83, -102.37) * mm, "construction": true});
            skLineSegment(sketch, "E204.top", {"start": v(-279.89, -94.43) * mm, "end": v(-287.83, -94.43) * mm, "construction": true});
            skLineSegment(sketch, "E204.left", {"start": v(-279.89, -102.37) * mm, "end": v(-279.89, -94.43) * mm, "construction": true});
            skLineSegment(sketch, "E204.right", {"start": v(-287.83, -102.37) * mm, "end": v(-287.83, -94.43) * mm, "construction": true});
            skCircle(sketch, "E205", {"center": v(-287.83, -94.43) * mm, "radius": 2.38 * mm});
            skCircle(sketch, "E206", {"center": v(-279.89, -94.43) * mm, "radius": 2.38 * mm});
            skCircle(sketch, "E207", {"center": v(-279.89, -102.37) * mm, "radius": 2.38 * mm});
            skCircle(sketch, "E208", {"center": v(-287.83, -102.37) * mm, "radius": 2.38 * mm});
            skLineSegment(sketch, "E209.bottom", {"start": v(-253.82, -3.36) * mm, "end": v(-269.7, -3.36) * mm});
            skLineSegment(sketch, "E209.top", {"start": v(-253.82, 12.51) * mm, "end": v(-269.7, 12.51) * mm});
            skLineSegment(sketch, "E209.left", {"start": v(-253.82, -3.36) * mm, "end": v(-253.82, 12.51) * mm});
            skLineSegment(sketch, "E209.right", {"start": v(-269.7, -3.36) * mm, "end": v(-269.7, 12.51) * mm});
            skPoint(sketch, "E209.middle", {"position": v(-261.75, 4.58) * mm});
            skLineSegment(sketch, "E210", {"start": v(-253.82, 4.58) * mm, "end": v(-269.7, 4.58) * mm, "construction": true});
            skLineSegment(sketch, "E211", {"start": v(-261.75, 12.51) * mm, "end": v(-261.75, -3.36) * mm, "construction": true});
            skLineSegment(sketch, "E212.bottom", {"start": v(-257.78, 0.6) * mm, "end": v(-265.72, 0.6) * mm, "construction": true});
            skLineSegment(sketch, "E212.top", {"start": v(-257.78, 8.54) * mm, "end": v(-265.72, 8.54) * mm, "construction": true});
            skLineSegment(sketch, "E212.left", {"start": v(-257.78, 0.6) * mm, "end": v(-257.78, 8.54) * mm, "construction": true});
            skLineSegment(sketch, "E212.right", {"start": v(-265.72, 0.6) * mm, "end": v(-265.72, 8.54) * mm, "construction": true});
            skCircle(sketch, "E213", {"center": v(-265.72, 8.54) * mm, "radius": 2.38 * mm});
            skCircle(sketch, "E214", {"center": v(-257.78, 8.54) * mm, "radius": 2.38 * mm});
            skCircle(sketch, "E215", {"center": v(-257.78, 0.6) * mm, "radius": 2.38 * mm});
            skCircle(sketch, "E216", {"center": v(-265.72, 0.6) * mm, "radius": 2.38 * mm});
            skLineSegment(sketch, "E217.bottom", {"start": v(-237.94, -3.36) * mm, "end": v(-253.82, -3.36) * mm});
            skLineSegment(sketch, "E217.top", {"start": v(-237.94, 12.51) * mm, "end": v(-253.82, 12.51) * mm});
            skPoint(sketch, "E217.middle", {"position": v(-245.88, 4.58) * mm});
            skLineSegment(sketch, "E218", {"start": v(-237.94, 4.58) * mm, "end": v(-253.82, 4.58) * mm, "construction": true});
            skLineSegment(sketch, "E219", {"start": v(-245.88, 12.51) * mm, "end": v(-245.88, -3.36) * mm, "construction": true});
            skLineSegment(sketch, "E220.bottom", {"start": v(-241.9, 0.6) * mm, "end": v(-249.85, 0.6) * mm, "construction": true});
            skLineSegment(sketch, "E220.top", {"start": v(-241.9, 8.54) * mm, "end": v(-249.85, 8.54) * mm, "construction": true});
            skLineSegment(sketch, "E220.left", {"start": v(-241.9, 0.6) * mm, "end": v(-241.9, 8.54) * mm, "construction": true});
            skLineSegment(sketch, "E220.right", {"start": v(-249.85, 0.6) * mm, "end": v(-249.85, 8.54) * mm, "construction": true});
            skCircle(sketch, "E221", {"center": v(-249.85, 8.54) * mm, "radius": 2.38 * mm});
            skCircle(sketch, "E222", {"center": v(-241.9, 8.54) * mm, "radius": 2.38 * mm});
            skCircle(sketch, "E223", {"center": v(-241.9, 0.6) * mm, "radius": 2.38 * mm});
            skCircle(sketch, "E224", {"center": v(-249.85, 0.6) * mm, "radius": 2.38 * mm});
            skLineSegment(sketch, "E225.bottom", {"start": v(-154, -21.78) * mm, "end": v(-161.92, -21.78) * mm});
            skLineSegment(sketch, "E225.left", {"start": v(-154, -21.78) * mm, "end": v(-154, -5.9) * mm});
            skLineSegment(sketch, "E225.right", {"start": v(-161.92, -21.78) * mm, "end": v(-161.92, -5.9) * mm});
            skPoint(sketch, "E225.middle", {"position": v(-157.96, -13.84) * mm});
            skLineSegment(sketch, "E226", {"start": v(-157.96, -5.9) * mm, "end": v(-157.96, -21.78) * mm, "construction": true});
            skLineSegment(sketch, "E227", {"start": v(-161.92, -13.84) * mm, "end": v(-154, -13.84) * mm, "construction": true});
            skLineSegment(sketch, "E228", {"start": v(-161.92, -17.65) * mm, "end": v(-154, -17.65) * mm, "construction": true});
            skLineSegment(sketch, "E229", {"start": v(-161.92, -10.04) * mm, "end": v(-154, -10.04) * mm, "construction": true});
            skCircle(sketch, "E230", {"center": v(-157.96, -10.04) * mm, "radius": 2.38 * mm});
            skCircle(sketch, "E231", {"center": v(-157.96, -17.65) * mm, "radius": 2.38 * mm});
            skSolve(sketch);
        }
        {
            var Q0;
            Q0=makeQuery(id+"F0.imprint","IMPRINT",FACE,{"disambiguationData":[TD([[makeQuery(id+"F0.imprint","IMPRINT",EDGE,{"derivedFrom":sQuery(id+"F0.wireOp",EDGE,"E0.bottom")}),-1.0]])]});
            var Q1;
            Q1=makeQuery(id+"F0.imprint","IMPRINT",FACE,{"disambiguationData":[TD([[makeQuery(id+"F0.imprint","IMPRINT",EDGE,{"derivedFrom":sQuery(id+"F0.wireOp",EDGE,"E7")}),1.0]])]});
            var Q2;
            Q2=makeQuery(id+"F0.imprint","IMPRINT",FACE,{"disambiguationData":[TD([[makeQuery(id+"F0.imprint","IMPRINT",EDGE,{"derivedFrom":sQuery(id+"F0.wireOp",EDGE,"E4")}),1.0]])]});
            var Q3;
            Q3=makeQuery(id+"F0.imprint","IMPRINT",FACE,{"disambiguationData":[TD([[makeQuery(id+"F0.imprint","IMPRINT",EDGE,{"derivedFrom":sQuery(id+"F0.wireOp",EDGE,"E5")}),1.0]])]});
            var Q4;
            Q4=makeQuery(id+"F0.imprint","IMPRINT",FACE,{"disambiguationData":[TD([[makeQuery(id+"F0.imprint","IMPRINT",EDGE,{"derivedFrom":sQuery(id+"F0.wireOp",EDGE,"E6")}),1.0]])]});
            extrude(context, id + "F1", {"entities" : qUnion([Q0, Q1, Q2, Q3, Q4]), "depth" : 9.52 * mm, "offsetDistance" : 25.4 * mm});
        }
        {
            var Q0;
            Q0=makeQuery(id+"F0.imprint","IMPRINT",FACE,{"disambiguationData":[TD([[makeQuery(id+"F0.imprint","IMPRINT",EDGE,{"derivedFrom":sQuery(id+"F0.wireOp",EDGE,"E7")}),1.0]])]});
            var Q1;
            Q1=makeQuery(id+"F0.imprint","IMPRINT",FACE,{"disambiguationData":[TD([[makeQuery(id+"F0.imprint","IMPRINT",EDGE,{"derivedFrom":sQuery(id+"F0.wireOp",EDGE,"E6")}),1.0]])]});
            var Q2;
            Q2=makeQuery(id+"F0.imprint","IMPRINT",FACE,{"disambiguationData":[TD([[makeQuery(id+"F0.imprint","IMPRINT",EDGE,{"derivedFrom":sQuery(id+"F0.wireOp",EDGE,"E4")}),1.0]])]});
            var Q3;
            Q3=makeQuery(id+"F0.imprint","IMPRINT",FACE,{"disambiguationData":[TD([[makeQuery(id+"F0.imprint","IMPRINT",EDGE,{"derivedFrom":sQuery(id+"F0.wireOp",EDGE,"E5")}),1.0]])]});
            extrude(context, id + "F2", {"entities" : qUnion([Q0, Q1, Q2, Q3]), "operationType" : NewBodyOperationType.ADD, "oppositeDirection" : true, "depth" : 1.59 * mm, "offsetDistance" : 25.4 * mm});
        }
        {
            var Q0;
            Q0=makeQuery(id+"F1.opExtrude","CAP_FACE",FACE,{"disambiguationData":[OSD([sQuery(id+"F0.wireOp",EDGE,"E0.bottom"),sQuery(id+"F0.wireOp",EDGE,"E0.top"),sQuery(id+"F0.wireOp",EDGE,"E0.left"),sQuery(id+"F0.wireOp",EDGE,"E0.right")])],"isStart":false});
            shell(context, id + "F3", {"entities" : qUnion([Q0]), "thickness" : 1.59 * mm});
        }
        {
            var Q0;
            Q0=makeQuery(id+"F0.imprint","IMPRINT",FACE,{"disambiguationData":[TD([[makeQuery(id+"F0.imprint","IMPRINT",EDGE,{"derivedFrom":sQuery(id+"F0.wireOp",EDGE,"E20")}),1.0]])]});
            var Q1;
            Q1=makeQuery(id+"F0.imprint","IMPRINT",FACE,{"disambiguationData":[TD([[makeQuery(id+"F0.imprint","IMPRINT",EDGE,{"derivedFrom":sQuery(id+"F0.wireOp",EDGE,"E23")}),1.0]])]});
            var Q2;
            Q2=makeQuery(id+"F0.imprint","IMPRINT",FACE,{"disambiguationData":[TD([[makeQuery(id+"F0.imprint","IMPRINT",EDGE,{"derivedFrom":sQuery(id+"F0.wireOp",EDGE,"E22")}),1.0]])]});
            var Q3;
            Q3=makeQuery(id+"F0.imprint","IMPRINT",FACE,{"disambiguationData":[TD([[makeQuery(id+"F0.imprint","IMPRINT",EDGE,{"derivedFrom":sQuery(id+"F0.wireOp",EDGE,"E14")}),1.0]])]});
            var Q4;
            Q4=makeQuery(id+"F0.imprint","IMPRINT",FACE,{"disambiguationData":[TD([[makeQuery(id+"F0.imprint","IMPRINT",EDGE,{"derivedFrom":sQuery(id+"F0.wireOp",EDGE,"E12")}),1.0]])]});
            var Q5;
            Q5=makeQuery(id+"F0.imprint","IMPRINT",FACE,{"disambiguationData":[TD([[makeQuery(id+"F0.imprint","IMPRINT",EDGE,{"derivedFrom":sQuery(id+"F0.wireOp",EDGE,"E16.bottom")}),-1.0]])]});
            var Q6;
            Q6=makeQuery(id+"F0.imprint","IMPRINT",FACE,{"disambiguationData":[TD([[makeQuery(id+"F0.imprint","IMPRINT",EDGE,{"derivedFrom":sQuery(id+"F0.wireOp",EDGE,"E15")}),1.0]])]});
            var Q7;
            Q7=makeQuery(id+"F0.imprint","IMPRINT",FACE,{"disambiguationData":[TD([[makeQuery(id+"F0.imprint","IMPRINT",EDGE,{"derivedFrom":sQuery(id+"F0.wireOp",EDGE,"E21")}),1.0]])]});
            var Q8;
            Q8=makeQuery(id+"F0.imprint","IMPRINT",FACE,{"disambiguationData":[TD([[makeQuery(id+"F0.imprint","IMPRINT",EDGE,{"derivedFrom":sQuery(id+"F0.wireOp",EDGE,"E8.bottom")}),-1.0]])]});
            var Q9;
            Q9=makeQuery(id+"F0.imprint","IMPRINT",FACE,{"disambiguationData":[TD([[makeQuery(id+"F0.imprint","IMPRINT",EDGE,{"derivedFrom":sQuery(id+"F0.wireOp",EDGE,"E13")}),1.0]])]});
            extrude(context, id + "F4", {"entities" : qUnion([Q0, Q1, Q2, Q3, Q4, Q5, Q6, Q7, Q8, Q9]), "depth" : 3.17 * mm, "offsetDistance" : 25.4 * mm});
        }
        {
            var Q0;
            Q0=makeQuery(id+"F0.imprint","IMPRINT",FACE,{"disambiguationData":[TD([[makeQuery(id+"F0.imprint","IMPRINT",EDGE,{"derivedFrom":sQuery(id+"F0.wireOp",EDGE,"E15")}),1.0]])]});
            var Q1;
            Q1=makeQuery(id+"F0.imprint","IMPRINT",FACE,{"disambiguationData":[TD([[makeQuery(id+"F0.imprint","IMPRINT",EDGE,{"derivedFrom":sQuery(id+"F0.wireOp",EDGE,"E21")}),1.0]])]});
            var Q2;
            Q2=makeQuery(id+"F0.imprint","IMPRINT",FACE,{"disambiguationData":[TD([[makeQuery(id+"F0.imprint","IMPRINT",EDGE,{"derivedFrom":sQuery(id+"F0.wireOp",EDGE,"E14")}),1.0]])]});
            var Q3;
            Q3=makeQuery(id+"F0.imprint","IMPRINT",FACE,{"disambiguationData":[TD([[makeQuery(id+"F0.imprint","IMPRINT",EDGE,{"derivedFrom":sQuery(id+"F0.wireOp",EDGE,"E12")}),1.0]])]});
            var Q4;
            Q4=makeQuery(id+"F0.imprint","IMPRINT",FACE,{"disambiguationData":[TD([[makeQuery(id+"F0.imprint","IMPRINT",EDGE,{"derivedFrom":sQuery(id+"F0.wireOp",EDGE,"E23")}),1.0]])]});
            var Q5;
            Q5=makeQuery(id+"F0.imprint","IMPRINT",FACE,{"disambiguationData":[TD([[makeQuery(id+"F0.imprint","IMPRINT",EDGE,{"derivedFrom":sQuery(id+"F0.wireOp",EDGE,"E22")}),1.0]])]});
            var Q6;
            Q6=makeQuery(id+"F0.imprint","IMPRINT",FACE,{"disambiguationData":[TD([[makeQuery(id+"F0.imprint","IMPRINT",EDGE,{"derivedFrom":sQuery(id+"F0.wireOp",EDGE,"E13")}),1.0]])]});
            var Q7;
            Q7=makeQuery(id+"F0.imprint","IMPRINT",FACE,{"disambiguationData":[TD([[makeQuery(id+"F0.imprint","IMPRINT",EDGE,{"derivedFrom":sQuery(id+"F0.wireOp",EDGE,"E20")}),1.0]])]});
            extrude(context, id + "F5", {"entities" : qUnion([Q0, Q1, Q2, Q3, Q4, Q5, Q6, Q7]), "operationType" : NewBodyOperationType.ADD, "oppositeDirection" : true, "depth" : 1.59 * mm, "offsetDistance" : 25.4 * mm});
        }
        {
            var Q0;
            Q0=makeQuery(id+"F4.opExtrude","CAP_FACE",FACE,{"disambiguationData":[OSD([sQuery(id+"F0.wireOp",EDGE,"E8.bottom"),sQuery(id+"F0.wireOp",EDGE,"E8.top"),sQuery(id+"F0.wireOp",EDGE,"E8.right"),sQuery(id+"F0.wireOp",EDGE,"E16.bottom"),sQuery(id+"F0.wireOp",EDGE,"E16.top"),sQuery(id+"F0.wireOp",EDGE,"E16.left")])],"isStart":false});
            shell(context, id + "F6", {"entities" : qUnion([Q0]), "thickness" : 1.59 * mm});
        }
        {
            var Q0;
            Q0=makeQuery(id+"F0.imprint","IMPRINT",FACE,{"disambiguationData":[TD([[makeQuery(id+"F0.imprint","IMPRINT",EDGE,{"derivedFrom":sQuery(id+"F0.wireOp",EDGE,"E168")}),1.0]])]});
            var Q1;
            Q1=makeQuery(id+"F0.imprint","IMPRINT",FACE,{"disambiguationData":[TD([[makeQuery(id+"F0.imprint","IMPRINT",EDGE,{"derivedFrom":sQuery(id+"F0.wireOp",EDGE,"E29")}),1.0]])]});
            var Q2;
            Q2=makeQuery(id+"F0.imprint","IMPRINT",FACE,{"disambiguationData":[TD([[makeQuery(id+"F0.imprint","IMPRINT",EDGE,{"derivedFrom":sQuery(id+"F0.wireOp",EDGE,"E169")}),1.0]])]});
            var Q3;
            Q3=makeQuery(id+"F0.imprint","IMPRINT",FACE,{"disambiguationData":[TD([[makeQuery(id+"F0.imprint","IMPRINT",EDGE,{"derivedFrom":sQuery(id+"F0.wireOp",EDGE,"E163")}),1.0]])]});
            var Q4;
            Q4=makeQuery(id+"F0.imprint","IMPRINT",FACE,{"disambiguationData":[TD([[makeQuery(id+"F0.imprint","IMPRINT",EDGE,{"derivedFrom":sQuery(id+"F0.wireOp",EDGE,"E39.bottom")}),-1.0]])]});
            var Q5;
            Q5=makeQuery(id+"F0.imprint","IMPRINT",FACE,{"disambiguationData":[TD([[makeQuery(id+"F0.imprint","IMPRINT",EDGE,{"derivedFrom":sQuery(id+"F0.wireOp",EDGE,"E162")}),1.0]])]});
            var Q6;
            {var subQ0=sQuery(id+"F0.wireOp",EDGE,"E155.right");Q6=makeQuery(id+"F0.imprint","IMPRINT",FACE,{"disambiguationData":[TD([[makeQuery(id+"F0.imprint","IMPRINT",EDGE,{"derivedFrom":subQ0}),1.0]])]});}
            var Q7;
            Q7=makeQuery(id+"F0.imprint","IMPRINT",FACE,{"disambiguationData":[TD([[makeQuery(id+"F0.imprint","IMPRINT",EDGE,{"derivedFrom":sQuery(id+"F0.wireOp",EDGE,"E24.bottom")}),-1.0]])]});
            var Q8;
            Q8=makeQuery(id+"F0.imprint","IMPRINT",FACE,{"disambiguationData":[TD([[makeQuery(id+"F0.imprint","IMPRINT",EDGE,{"derivedFrom":sQuery(id+"F0.wireOp",EDGE,"E165")}),1.0]])]});
            var Q9;
            Q9=makeQuery(id+"F0.imprint","IMPRINT",FACE,{"disambiguationData":[TD([[makeQuery(id+"F0.imprint","IMPRINT",EDGE,{"derivedFrom":sQuery(id+"F0.wireOp",EDGE,"E53")}),1.0]])]});
            var Q10;
            Q10=makeQuery(id+"F0.imprint","IMPRINT",FACE,{"disambiguationData":[TD([[makeQuery(id+"F0.imprint","IMPRINT",EDGE,{"derivedFrom":sQuery(id+"F0.wireOp",EDGE,"E43")}),1.0]])]});
            var Q11;
            {var subQ1=sQuery(id+"F0.wireOp",EDGE,"E47.left");Q11=makeQuery(id+"F0.imprint","IMPRINT",FACE,{"disambiguationData":[TD([[makeQuery(id+"F0.imprint","IMPRINT",EDGE,{"derivedFrom":subQ1}),-1.0]])]});}
            var Q12;
            Q12=makeQuery(id+"F0.imprint","IMPRINT",FACE,{"disambiguationData":[TD([[makeQuery(id+"F0.imprint","IMPRINT",EDGE,{"derivedFrom":sQuery(id+"F0.wireOp",EDGE,"E45")}),1.0]])]});
            var Q13;
            Q13=makeQuery(id+"F0.imprint","IMPRINT",FACE,{"disambiguationData":[TD([[makeQuery(id+"F0.imprint","IMPRINT",EDGE,{"derivedFrom":sQuery(id+"F0.wireOp",EDGE,"E51")}),1.0]])]});
            var Q14;
            Q14=makeQuery(id+"F0.imprint","IMPRINT",FACE,{"disambiguationData":[TD([[makeQuery(id+"F0.imprint","IMPRINT",EDGE,{"derivedFrom":sQuery(id+"F0.wireOp",EDGE,"E166")}),1.0]])]});
            var Q15;
            Q15=makeQuery(id+"F0.imprint","IMPRINT",FACE,{"disambiguationData":[TD([[makeQuery(id+"F0.imprint","IMPRINT",EDGE,{"derivedFrom":sQuery(id+"F0.wireOp",EDGE,"E47.bottom")}),-1.0]])]});
            var Q16;
            Q16=makeQuery(id+"F0.imprint","IMPRINT",FACE,{"disambiguationData":[TD([[makeQuery(id+"F0.imprint","IMPRINT",EDGE,{"derivedFrom":sQuery(id+"F0.wireOp",EDGE,"E44")}),1.0]])]});
            var Q17;
            Q17=makeQuery(id+"F0.imprint","IMPRINT",FACE,{"disambiguationData":[TD([[makeQuery(id+"F0.imprint","IMPRINT",EDGE,{"derivedFrom":sQuery(id+"F0.wireOp",EDGE,"E30")}),1.0]])]});
            var Q18;
            Q18=makeQuery(id+"F0.imprint","IMPRINT",FACE,{"disambiguationData":[TD([[makeQuery(id+"F0.imprint","IMPRINT",EDGE,{"derivedFrom":sQuery(id+"F0.wireOp",EDGE,"E167")}),1.0]])]});
            var Q19;
            Q19=makeQuery(id+"F0.imprint","IMPRINT",FACE,{"disambiguationData":[TD([[makeQuery(id+"F0.imprint","IMPRINT",EDGE,{"derivedFrom":sQuery(id+"F0.wireOp",EDGE,"E164")}),1.0]])]});
            var Q20;
            Q20=makeQuery(id+"F0.imprint","IMPRINT",FACE,{"disambiguationData":[TD([[makeQuery(id+"F0.imprint","IMPRINT",EDGE,{"derivedFrom":sQuery(id+"F0.wireOp",EDGE,"E54")}),1.0]])]});
            var Q21;
            Q21=makeQuery(id+"F0.imprint","IMPRINT",FACE,{"disambiguationData":[TD([[makeQuery(id+"F0.imprint","IMPRINT",EDGE,{"derivedFrom":sQuery(id+"F0.wireOp",EDGE,"E52")}),1.0]])]});
            var Q22;
            Q22=makeQuery(id+"F0.imprint","IMPRINT",FACE,{"disambiguationData":[TD([[makeQuery(id+"F0.imprint","IMPRINT",EDGE,{"derivedFrom":sQuery(id+"F0.wireOp",EDGE,"E46")}),1.0]])]});
            extrude(context, id + "F7", {"entities" : qUnion([Q0, Q1, Q2, Q3, Q4, Q5, Q6, Q7, Q8, Q9, Q10, Q11, Q12, Q13, Q14, Q15, Q16, Q17, Q18, Q19, Q20, Q21, Q22]), "depth" : 9.52 * mm, "offsetDistance" : 25.4 * mm});
        }
        {
            var Q0;
            Q0=makeQuery(id+"F0.imprint","IMPRINT",FACE,{"disambiguationData":[TD([[makeQuery(id+"F0.imprint","IMPRINT",EDGE,{"derivedFrom":sQuery(id+"F0.wireOp",EDGE,"E115")}),1.0]])]});
            var Q1;
            Q1=makeQuery(id+"F0.imprint","IMPRINT",FACE,{"disambiguationData":[TD([[makeQuery(id+"F0.imprint","IMPRINT",EDGE,{"derivedFrom":sQuery(id+"F0.wireOp",EDGE,"E109.bottom")}),-1.0]])]});
            var Q2;
            Q2=makeQuery(id+"F0.imprint","IMPRINT",FACE,{"disambiguationData":[TD([[makeQuery(id+"F0.imprint","IMPRINT",EDGE,{"derivedFrom":sQuery(id+"F0.wireOp",EDGE,"E105")}),1.0]])]});
            var Q3;
            Q3=makeQuery(id+"F0.imprint","IMPRINT",FACE,{"disambiguationData":[TD([[makeQuery(id+"F0.imprint","IMPRINT",EDGE,{"derivedFrom":sQuery(id+"F0.wireOp",EDGE,"E113")}),1.0]])]});
            var Q4;
            Q4=makeQuery(id+"F0.imprint","IMPRINT",FACE,{"disambiguationData":[TD([[makeQuery(id+"F0.imprint","IMPRINT",EDGE,{"derivedFrom":sQuery(id+"F0.wireOp",EDGE,"E101.bottom")}),-1.0]])]});
            var Q5;
            Q5=makeQuery(id+"F0.imprint","IMPRINT",FACE,{"disambiguationData":[TD([[makeQuery(id+"F0.imprint","IMPRINT",EDGE,{"derivedFrom":sQuery(id+"F0.wireOp",EDGE,"E107")}),1.0]])]});
            var Q6;
            Q6=makeQuery(id+"F0.imprint","IMPRINT",FACE,{"disambiguationData":[TD([[makeQuery(id+"F0.imprint","IMPRINT",EDGE,{"derivedFrom":sQuery(id+"F0.wireOp",EDGE,"E116")}),1.0]])]});
            var Q7;
            Q7=makeQuery(id+"F0.imprint","IMPRINT",FACE,{"disambiguationData":[TD([[makeQuery(id+"F0.imprint","IMPRINT",EDGE,{"derivedFrom":sQuery(id+"F0.wireOp",EDGE,"E108")}),1.0]])]});
            var Q8;
            Q8=makeQuery(id+"F0.imprint","IMPRINT",FACE,{"disambiguationData":[TD([[makeQuery(id+"F0.imprint","IMPRINT",EDGE,{"derivedFrom":sQuery(id+"F0.wireOp",EDGE,"E106")}),1.0]])]});
            var Q9;
            Q9=makeQuery(id+"F0.imprint","IMPRINT",FACE,{"disambiguationData":[TD([[makeQuery(id+"F0.imprint","IMPRINT",EDGE,{"derivedFrom":sQuery(id+"F0.wireOp",EDGE,"E114")}),1.0]])]});
            extrude(context, id + "F8", {"entities" : qUnion([Q0, Q1, Q2, Q3, Q4, Q5, Q6, Q7, Q8, Q9]), "depth" : 9.52 * mm, "offsetDistance" : 25.4 * mm});
        }
        {
            var Q0;
            Q0=makeQuery(id+"F0.imprint","IMPRINT",FACE,{"disambiguationData":[TD([[makeQuery(id+"F0.imprint","IMPRINT",EDGE,{"derivedFrom":sQuery(id+"F0.wireOp",EDGE,"E106")}),1.0]])]});
            var Q1;
            Q1=makeQuery(id+"F0.imprint","IMPRINT",FACE,{"disambiguationData":[TD([[makeQuery(id+"F0.imprint","IMPRINT",EDGE,{"derivedFrom":sQuery(id+"F0.wireOp",EDGE,"E116")}),1.0]])]});
            var Q2;
            Q2=makeQuery(id+"F0.imprint","IMPRINT",FACE,{"disambiguationData":[TD([[makeQuery(id+"F0.imprint","IMPRINT",EDGE,{"derivedFrom":sQuery(id+"F0.wireOp",EDGE,"E108")}),1.0]])]});
            var Q3;
            Q3=makeQuery(id+"F0.imprint","IMPRINT",FACE,{"disambiguationData":[TD([[makeQuery(id+"F0.imprint","IMPRINT",EDGE,{"derivedFrom":sQuery(id+"F0.wireOp",EDGE,"E113")}),1.0]])]});
            var Q4;
            Q4=makeQuery(id+"F0.imprint","IMPRINT",FACE,{"disambiguationData":[TD([[makeQuery(id+"F0.imprint","IMPRINT",EDGE,{"derivedFrom":sQuery(id+"F0.wireOp",EDGE,"E115")}),1.0]])]});
            var Q5;
            Q5=makeQuery(id+"F0.imprint","IMPRINT",FACE,{"disambiguationData":[TD([[makeQuery(id+"F0.imprint","IMPRINT",EDGE,{"derivedFrom":sQuery(id+"F0.wireOp",EDGE,"E105")}),1.0]])]});
            var Q6;
            Q6=makeQuery(id+"F0.imprint","IMPRINT",FACE,{"disambiguationData":[TD([[makeQuery(id+"F0.imprint","IMPRINT",EDGE,{"derivedFrom":sQuery(id+"F0.wireOp",EDGE,"E107")}),1.0]])]});
            var Q7;
            Q7=makeQuery(id+"F0.imprint","IMPRINT",FACE,{"disambiguationData":[TD([[makeQuery(id+"F0.imprint","IMPRINT",EDGE,{"derivedFrom":sQuery(id+"F0.wireOp",EDGE,"E114")}),1.0]])]});
            extrude(context, id + "F9", {"entities" : qUnion([Q0, Q1, Q2, Q3, Q4, Q5, Q6, Q7]), "operationType" : NewBodyOperationType.ADD, "oppositeDirection" : true, "depth" : 1.59 * mm, "offsetDistance" : 25.4 * mm});
        }
        {
            var Q0;
            Q0=makeQuery(id+"F0.imprint","IMPRINT",FACE,{"disambiguationData":[TD([[makeQuery(id+"F0.imprint","IMPRINT",EDGE,{"derivedFrom":sQuery(id+"F0.wireOp",EDGE,"E29")}),1.0]])]});
            var Q1;
            Q1=makeQuery(id+"F0.imprint","IMPRINT",FACE,{"disambiguationData":[TD([[makeQuery(id+"F0.imprint","IMPRINT",EDGE,{"derivedFrom":sQuery(id+"F0.wireOp",EDGE,"E30")}),1.0]])]});
            extrude(context, id + "F10", {"entities" : qUnion([Q0, Q1]), "operationType" : NewBodyOperationType.ADD, "oppositeDirection" : true, "depth" : 1.59 * mm, "offsetDistance" : 25.4 * mm});
        }
        {
            var Q0;
            Q0=makeQuery(id+"F0.imprint","IMPRINT",FACE,{"disambiguationData":[TD([[makeQuery(id+"F0.imprint","IMPRINT",EDGE,{"derivedFrom":sQuery(id+"F0.wireOp",EDGE,"E45")}),1.0]])]});
            var Q1;
            Q1=makeQuery(id+"F0.imprint","IMPRINT",FACE,{"disambiguationData":[TD([[makeQuery(id+"F0.imprint","IMPRINT",EDGE,{"derivedFrom":sQuery(id+"F0.wireOp",EDGE,"E43")}),1.0]])]});
            var Q2;
            Q2=makeQuery(id+"F0.imprint","IMPRINT",FACE,{"disambiguationData":[TD([[makeQuery(id+"F0.imprint","IMPRINT",EDGE,{"derivedFrom":sQuery(id+"F0.wireOp",EDGE,"E168")}),1.0]])]});
            var Q3;
            Q3=makeQuery(id+"F0.imprint","IMPRINT",FACE,{"disambiguationData":[TD([[makeQuery(id+"F0.imprint","IMPRINT",EDGE,{"derivedFrom":sQuery(id+"F0.wireOp",EDGE,"E169")}),1.0]])]});
            var Q4;
            Q4=makeQuery(id+"F0.imprint","IMPRINT",FACE,{"disambiguationData":[TD([[makeQuery(id+"F0.imprint","IMPRINT",EDGE,{"derivedFrom":sQuery(id+"F0.wireOp",EDGE,"E44")}),1.0]])]});
            var Q5;
            Q5=makeQuery(id+"F0.imprint","IMPRINT",FACE,{"disambiguationData":[TD([[makeQuery(id+"F0.imprint","IMPRINT",EDGE,{"derivedFrom":sQuery(id+"F0.wireOp",EDGE,"E164")}),1.0]])]});
            var Q6;
            Q6=makeQuery(id+"F0.imprint","IMPRINT",FACE,{"disambiguationData":[TD([[makeQuery(id+"F0.imprint","IMPRINT",EDGE,{"derivedFrom":sQuery(id+"F0.wireOp",EDGE,"E54")}),1.0]])]});
            var Q7;
            Q7=makeQuery(id+"F0.imprint","IMPRINT",FACE,{"disambiguationData":[TD([[makeQuery(id+"F0.imprint","IMPRINT",EDGE,{"derivedFrom":sQuery(id+"F0.wireOp",EDGE,"E167")}),1.0]])]});
            var Q8;
            Q8=makeQuery(id+"F0.imprint","IMPRINT",FACE,{"disambiguationData":[TD([[makeQuery(id+"F0.imprint","IMPRINT",EDGE,{"derivedFrom":sQuery(id+"F0.wireOp",EDGE,"E46")}),1.0]])]});
            var Q9;
            Q9=makeQuery(id+"F0.imprint","IMPRINT",FACE,{"disambiguationData":[TD([[makeQuery(id+"F0.imprint","IMPRINT",EDGE,{"derivedFrom":sQuery(id+"F0.wireOp",EDGE,"E162")}),1.0]])]});
            var Q10;
            Q10=makeQuery(id+"F0.imprint","IMPRINT",FACE,{"disambiguationData":[TD([[makeQuery(id+"F0.imprint","IMPRINT",EDGE,{"derivedFrom":sQuery(id+"F0.wireOp",EDGE,"E163")}),1.0]])]});
            var Q11;
            Q11=makeQuery(id+"F0.imprint","IMPRINT",FACE,{"disambiguationData":[TD([[makeQuery(id+"F0.imprint","IMPRINT",EDGE,{"derivedFrom":sQuery(id+"F0.wireOp",EDGE,"E166")}),1.0]])]});
            var Q12;
            Q12=makeQuery(id+"F0.imprint","IMPRINT",FACE,{"disambiguationData":[TD([[makeQuery(id+"F0.imprint","IMPRINT",EDGE,{"derivedFrom":sQuery(id+"F0.wireOp",EDGE,"E52")}),1.0]])]});
            var Q13;
            Q13=makeQuery(id+"F0.imprint","IMPRINT",FACE,{"disambiguationData":[TD([[makeQuery(id+"F0.imprint","IMPRINT",EDGE,{"derivedFrom":sQuery(id+"F0.wireOp",EDGE,"E53")}),1.0]])]});
            var Q14;
            Q14=makeQuery(id+"F0.imprint","IMPRINT",FACE,{"disambiguationData":[TD([[makeQuery(id+"F0.imprint","IMPRINT",EDGE,{"derivedFrom":sQuery(id+"F0.wireOp",EDGE,"E165")}),1.0]])]});
            var Q15;
            Q15=makeQuery(id+"F0.imprint","IMPRINT",FACE,{"disambiguationData":[TD([[makeQuery(id+"F0.imprint","IMPRINT",EDGE,{"derivedFrom":sQuery(id+"F0.wireOp",EDGE,"E51")}),1.0]])]});
            extrude(context, id + "F11", {"entities" : qUnion([Q0, Q1, Q2, Q3, Q4, Q5, Q6, Q7, Q8, Q9, Q10, Q11, Q12, Q13, Q14, Q15]), "operationType" : NewBodyOperationType.ADD, "oppositeDirection" : true, "depth" : 1.59 * mm, "offsetDistance" : 25.4 * mm});
        }
        {
            var Q0;
            Q0=makeQuery(id+"F0.imprint","IMPRINT",FACE,{"disambiguationData":[TD([[makeQuery(id+"F0.imprint","IMPRINT",EDGE,{"derivedFrom":sQuery(id+"F0.wireOp",EDGE,"E132.bottom")}),-1.0]])]});
            var Q1;
            Q1=makeQuery(id+"F0.imprint","IMPRINT",FACE,{"disambiguationData":[TD([[makeQuery(id+"F0.imprint","IMPRINT",EDGE,{"derivedFrom":sQuery(id+"F0.wireOp",EDGE,"E60")}),1.0]])]});
            var Q2;
            Q2=makeQuery(id+"F0.imprint","IMPRINT",FACE,{"disambiguationData":[TD([[makeQuery(id+"F0.imprint","IMPRINT",EDGE,{"derivedFrom":sQuery(id+"F0.wireOp",EDGE,"E83")}),1.0]])]});
            var Q3;
            Q3=makeQuery(id+"F0.imprint","IMPRINT",FACE,{"disambiguationData":[TD([[makeQuery(id+"F0.imprint","IMPRINT",EDGE,{"derivedFrom":sQuery(id+"F0.wireOp",EDGE,"E145")}),1.0]])]});
            var Q4;
            Q4=makeQuery(id+"F0.imprint","IMPRINT",FACE,{"disambiguationData":[TD([[makeQuery(id+"F0.imprint","IMPRINT",EDGE,{"derivedFrom":sQuery(id+"F0.wireOp",EDGE,"E122")}),1.0]])]});
            var Q5;
            Q5=makeQuery(id+"F0.imprint","IMPRINT",FACE,{"disambiguationData":[TD([[makeQuery(id+"F0.imprint","IMPRINT",EDGE,{"derivedFrom":sQuery(id+"F0.wireOp",EDGE,"E67")}),1.0]])]});
            var Q6;
            Q6=makeQuery(id+"F0.imprint","IMPRINT",FACE,{"disambiguationData":[TD([[makeQuery(id+"F0.imprint","IMPRINT",EDGE,{"derivedFrom":sQuery(id+"F0.wireOp",EDGE,"E130")}),1.0]])]});
            var Q7;
            Q7=makeQuery(id+"F0.imprint","IMPRINT",FACE,{"disambiguationData":[TD([[makeQuery(id+"F0.imprint","IMPRINT",EDGE,{"derivedFrom":sQuery(id+"F0.wireOp",EDGE,"E128")}),1.0]])]});
            var Q8;
            Q8=makeQuery(id+"F0.imprint","IMPRINT",FACE,{"disambiguationData":[TD([[makeQuery(id+"F0.imprint","IMPRINT",EDGE,{"derivedFrom":sQuery(id+"F0.wireOp",EDGE,"E77")}),1.0]])]});
            var Q9;
            Q9=makeQuery(id+"F0.imprint","IMPRINT",FACE,{"disambiguationData":[TD([[makeQuery(id+"F0.imprint","IMPRINT",EDGE,{"derivedFrom":sQuery(id+"F0.wireOp",EDGE,"E93.bottom")}),-1.0]])]});
            var Q10;
            Q10=makeQuery(id+"F0.imprint","IMPRINT",FACE,{"disambiguationData":[TD([[makeQuery(id+"F0.imprint","IMPRINT",EDGE,{"derivedFrom":sQuery(id+"F0.wireOp",EDGE,"E153")}),1.0]])]});
            var Q11;
            Q11=makeQuery(id+"F0.imprint","IMPRINT",FACE,{"disambiguationData":[TD([[makeQuery(id+"F0.imprint","IMPRINT",EDGE,{"derivedFrom":sQuery(id+"F0.wireOp",EDGE,"E84")}),1.0]])]});
            var Q12;
            Q12=makeQuery(id+"F0.imprint","IMPRINT",FACE,{"disambiguationData":[TD([[makeQuery(id+"F0.imprint","IMPRINT",EDGE,{"derivedFrom":sQuery(id+"F0.wireOp",EDGE,"E66")}),1.0]])]});
            var Q13;
            Q13=makeQuery(id+"F0.imprint","IMPRINT",FACE,{"disambiguationData":[TD([[makeQuery(id+"F0.imprint","IMPRINT",EDGE,{"derivedFrom":sQuery(id+"F0.wireOp",EDGE,"E69")}),1.0]])]});
            var Q14;
            Q14=makeQuery(id+"F0.imprint","IMPRINT",FACE,{"disambiguationData":[TD([[makeQuery(id+"F0.imprint","IMPRINT",EDGE,{"derivedFrom":sQuery(id+"F0.wireOp",EDGE,"E37")}),1.0]])]});
            var Q15;
            Q15=makeQuery(id+"F0.imprint","IMPRINT",FACE,{"disambiguationData":[TD([[makeQuery(id+"F0.imprint","IMPRINT",EDGE,{"derivedFrom":sQuery(id+"F0.wireOp",EDGE,"E85")}),1.0]])]});
            var Q16;
            Q16=makeQuery(id+"F0.imprint","IMPRINT",FACE,{"disambiguationData":[TD([[makeQuery(id+"F0.imprint","IMPRINT",EDGE,{"derivedFrom":sQuery(id+"F0.wireOp",EDGE,"E154")}),1.0]])]});
            var Q17;
            Q17=makeQuery(id+"F0.imprint","IMPRINT",FACE,{"disambiguationData":[TD([[makeQuery(id+"F0.imprint","IMPRINT",EDGE,{"derivedFrom":sQuery(id+"F0.wireOp",EDGE,"E78.top")}),1.0]])]});
            var Q18;
            Q18=makeQuery(id+"F0.imprint","IMPRINT",FACE,{"disambiguationData":[TD([[makeQuery(id+"F0.imprint","IMPRINT",EDGE,{"derivedFrom":sQuery(id+"F0.wireOp",EDGE,"E140.bottom")}),-1.0]])]});
            var Q19;
            Q19=makeQuery(id+"F0.imprint","IMPRINT",FACE,{"disambiguationData":[TD([[makeQuery(id+"F0.imprint","IMPRINT",EDGE,{"derivedFrom":sQuery(id+"F0.wireOp",EDGE,"E55.bottom")}),-1.0]])]});
            var Q20;
            Q20=makeQuery(id+"F0.imprint","IMPRINT",FACE,{"disambiguationData":[TD([[makeQuery(id+"F0.imprint","IMPRINT",EDGE,{"derivedFrom":sQuery(id+"F0.wireOp",EDGE,"E100")}),1.0]])]});
            var Q21;
            Q21=makeQuery(id+"F0.imprint","IMPRINT",FACE,{"disambiguationData":[TD([[makeQuery(id+"F0.imprint","IMPRINT",EDGE,{"derivedFrom":sQuery(id+"F0.wireOp",EDGE,"E144")}),1.0]])]});
            var Q22;
            Q22=makeQuery(id+"F0.imprint","IMPRINT",FACE,{"disambiguationData":[TD([[makeQuery(id+"F0.imprint","IMPRINT",EDGE,{"derivedFrom":sQuery(id+"F0.wireOp",EDGE,"E123")}),1.0]])]});
            var Q23;
            Q23=makeQuery(id+"F0.imprint","IMPRINT",FACE,{"disambiguationData":[TD([[makeQuery(id+"F0.imprint","IMPRINT",EDGE,{"derivedFrom":sQuery(id+"F0.wireOp",EDGE,"E82")}),1.0]])]});
            var Q24;
            Q24=makeQuery(id+"F0.imprint","IMPRINT",FACE,{"disambiguationData":[TD([[makeQuery(id+"F0.imprint","IMPRINT",EDGE,{"derivedFrom":sQuery(id+"F0.wireOp",EDGE,"E76")}),1.0]])]});
            var Q25;
            Q25=makeQuery(id+"F0.imprint","IMPRINT",FACE,{"disambiguationData":[TD([[makeQuery(id+"F0.imprint","IMPRINT",EDGE,{"derivedFrom":sQuery(id+"F0.wireOp",EDGE,"E35")}),1.0]])]});
            var Q26;
            Q26=makeQuery(id+"F0.imprint","IMPRINT",FACE,{"disambiguationData":[TD([[makeQuery(id+"F0.imprint","IMPRINT",EDGE,{"derivedFrom":sQuery(id+"F0.wireOp",EDGE,"E61")}),1.0]])]});
            var Q27;
            Q27=makeQuery(id+"F0.imprint","IMPRINT",FACE,{"disambiguationData":[TD([[makeQuery(id+"F0.imprint","IMPRINT",EDGE,{"derivedFrom":sQuery(id+"F0.wireOp",EDGE,"E136")}),1.0]])]});
            var Q28;
            Q28=makeQuery(id+"F0.imprint","IMPRINT",FACE,{"disambiguationData":[TD([[makeQuery(id+"F0.imprint","IMPRINT",EDGE,{"derivedFrom":sQuery(id+"F0.wireOp",EDGE,"E91")}),1.0]])]});
            var Q29;
            Q29=makeQuery(id+"F0.imprint","IMPRINT",FACE,{"disambiguationData":[TD([[makeQuery(id+"F0.imprint","IMPRINT",EDGE,{"derivedFrom":sQuery(id+"F0.wireOp",EDGE,"E124.bottom")}),-1.0]])]});
            var Q30;
            Q30=makeQuery(id+"F0.imprint","IMPRINT",FACE,{"disambiguationData":[TD([[makeQuery(id+"F0.imprint","IMPRINT",EDGE,{"derivedFrom":sQuery(id+"F0.wireOp",EDGE,"E70.top")}),1.0]])]});
            var Q31;
            Q31=makeQuery(id+"F0.imprint","IMPRINT",FACE,{"disambiguationData":[TD([[makeQuery(id+"F0.imprint","IMPRINT",EDGE,{"derivedFrom":sQuery(id+"F0.wireOp",EDGE,"E117.bottom")}),-1.0]])]});
            var Q32;
            Q32=makeQuery(id+"F0.imprint","IMPRINT",FACE,{"disambiguationData":[TD([[makeQuery(id+"F0.imprint","IMPRINT",EDGE,{"derivedFrom":sQuery(id+"F0.wireOp",EDGE,"E68")}),1.0]])]});
            var Q33;
            Q33=makeQuery(id+"F0.imprint","IMPRINT",FACE,{"disambiguationData":[TD([[makeQuery(id+"F0.imprint","IMPRINT",EDGE,{"derivedFrom":sQuery(id+"F0.wireOp",EDGE,"E62.top")}),1.0]])]});
            var Q34;
            Q34=makeQuery(id+"F0.imprint","IMPRINT",FACE,{"disambiguationData":[TD([[makeQuery(id+"F0.imprint","IMPRINT",EDGE,{"derivedFrom":sQuery(id+"F0.wireOp",EDGE,"E117.top")}),-1.0]])]});
            var Q35;
            Q35=makeQuery(id+"F0.imprint","IMPRINT",FACE,{"disambiguationData":[TD([[makeQuery(id+"F0.imprint","IMPRINT",EDGE,{"derivedFrom":sQuery(id+"F0.wireOp",EDGE,"E99")}),1.0]])]});
            var Q36;
            Q36=makeQuery(id+"F0.imprint","IMPRINT",FACE,{"disambiguationData":[TD([[makeQuery(id+"F0.imprint","IMPRINT",EDGE,{"derivedFrom":sQuery(id+"F0.wireOp",EDGE,"E36")}),1.0]])]});
            var Q37;
            Q37=makeQuery(id+"F0.imprint","IMPRINT",FACE,{"disambiguationData":[TD([[makeQuery(id+"F0.imprint","IMPRINT",EDGE,{"derivedFrom":sQuery(id+"F0.wireOp",EDGE,"E98")}),1.0]])]});
            var Q38;
            Q38=makeQuery(id+"F0.imprint","IMPRINT",FACE,{"disambiguationData":[TD([[makeQuery(id+"F0.imprint","IMPRINT",EDGE,{"derivedFrom":sQuery(id+"F0.wireOp",EDGE,"E137")}),1.0]])]});
            var Q39;
            Q39=makeQuery(id+"F0.imprint","IMPRINT",FACE,{"disambiguationData":[TD([[makeQuery(id+"F0.imprint","IMPRINT",EDGE,{"derivedFrom":sQuery(id+"F0.wireOp",EDGE,"E139")}),1.0]])]});
            var Q40;
            Q40=makeQuery(id+"F0.imprint","IMPRINT",FACE,{"disambiguationData":[TD([[makeQuery(id+"F0.imprint","IMPRINT",EDGE,{"derivedFrom":sQuery(id+"F0.wireOp",EDGE,"E147")}),1.0]])]});
            var Q41;
            Q41=makeQuery(id+"F0.imprint","IMPRINT",FACE,{"disambiguationData":[TD([[makeQuery(id+"F0.imprint","IMPRINT",EDGE,{"derivedFrom":sQuery(id+"F0.wireOp",EDGE,"E97")}),1.0]])]});
            var Q42;
            Q42=makeQuery(id+"F0.imprint","IMPRINT",FACE,{"disambiguationData":[TD([[makeQuery(id+"F0.imprint","IMPRINT",EDGE,{"derivedFrom":sQuery(id+"F0.wireOp",EDGE,"E131")}),1.0]])]});
            var Q43;
            Q43=makeQuery(id+"F0.imprint","IMPRINT",FACE,{"disambiguationData":[TD([[makeQuery(id+"F0.imprint","IMPRINT",EDGE,{"derivedFrom":sQuery(id+"F0.wireOp",EDGE,"E138")}),1.0]])]});
            var Q44;
            Q44=makeQuery(id+"F0.imprint","IMPRINT",FACE,{"disambiguationData":[TD([[makeQuery(id+"F0.imprint","IMPRINT",EDGE,{"derivedFrom":sQuery(id+"F0.wireOp",EDGE,"E86.top")}),1.0]])]});
            var Q45;
            Q45=makeQuery(id+"F0.imprint","IMPRINT",FACE,{"disambiguationData":[TD([[makeQuery(id+"F0.imprint","IMPRINT",EDGE,{"derivedFrom":sQuery(id+"F0.wireOp",EDGE,"E75")}),1.0]])]});
            var Q46;
            Q46=makeQuery(id+"F0.imprint","IMPRINT",FACE,{"disambiguationData":[TD([[makeQuery(id+"F0.imprint","IMPRINT",EDGE,{"derivedFrom":sQuery(id+"F0.wireOp",EDGE,"E146")}),1.0]])]});
            var Q47;
            Q47=makeQuery(id+"F0.imprint","IMPRINT",FACE,{"disambiguationData":[TD([[makeQuery(id+"F0.imprint","IMPRINT",EDGE,{"derivedFrom":sQuery(id+"F0.wireOp",EDGE,"E129")}),1.0]])]});
            var Q48;
            Q48=makeQuery(id+"F0.imprint","IMPRINT",FACE,{"disambiguationData":[TD([[makeQuery(id+"F0.imprint","IMPRINT",EDGE,{"derivedFrom":sQuery(id+"F0.wireOp",EDGE,"E92")}),1.0]])]});
            var Q49;
            Q49=makeQuery(id+"F0.imprint","IMPRINT",FACE,{"disambiguationData":[TD([[makeQuery(id+"F0.imprint","IMPRINT",EDGE,{"derivedFrom":sQuery(id+"F0.wireOp",EDGE,"E31.top")}),1.0]])]});
            var Q50;
            Q50=makeQuery(id+"F0.imprint","IMPRINT",FACE,{"disambiguationData":[TD([[makeQuery(id+"F0.imprint","IMPRINT",EDGE,{"derivedFrom":sQuery(id+"F0.wireOp",EDGE,"E38")}),1.0]])]});
            var Q51;
            Q51=makeQuery(id+"F0.imprint","IMPRINT",FACE,{"disambiguationData":[TD([[makeQuery(id+"F0.imprint","IMPRINT",EDGE,{"derivedFrom":sQuery(id+"F0.wireOp",EDGE,"E74")}),1.0]])]});
            extrude(context, id + "F12", {"entities" : qUnion([Q0, Q1, Q2, Q3, Q4, Q5, Q6, Q7, Q8, Q9, Q10, Q11, Q12, Q13, Q14, Q15, Q16, Q17, Q18, Q19, Q20, Q21, Q22, Q23, Q24, Q25, Q26, Q27, Q28, Q29, Q30, Q31, Q32, Q33, Q34, Q35, Q36, Q37, Q38, Q39, Q40, Q41, Q42, Q43, Q44, Q45, Q46, Q47, Q48, Q49, Q50, Q51]), "depth" : 3.17 * mm, "offsetDistance" : 25.4 * mm});
        }
        {
            var Q0;
            Q0=makeQuery(id+"F0.imprint","IMPRINT",FACE,{"disambiguationData":[TD([[makeQuery(id+"F0.imprint","IMPRINT",EDGE,{"derivedFrom":sQuery(id+"F0.wireOp",EDGE,"E77")}),1.0]])]});
            var Q1;
            Q1=makeQuery(id+"F0.imprint","IMPRINT",FACE,{"disambiguationData":[TD([[makeQuery(id+"F0.imprint","IMPRINT",EDGE,{"derivedFrom":sQuery(id+"F0.wireOp",EDGE,"E128")}),1.0]])]});
            var Q2;
            Q2=makeQuery(id+"F0.imprint","IMPRINT",FACE,{"disambiguationData":[TD([[makeQuery(id+"F0.imprint","IMPRINT",EDGE,{"derivedFrom":sQuery(id+"F0.wireOp",EDGE,"E66")}),1.0]])]});
            var Q3;
            Q3=makeQuery(id+"F0.imprint","IMPRINT",FACE,{"disambiguationData":[TD([[makeQuery(id+"F0.imprint","IMPRINT",EDGE,{"derivedFrom":sQuery(id+"F0.wireOp",EDGE,"E136")}),1.0]])]});
            var Q4;
            Q4=makeQuery(id+"F0.imprint","IMPRINT",FACE,{"disambiguationData":[TD([[makeQuery(id+"F0.imprint","IMPRINT",EDGE,{"derivedFrom":sQuery(id+"F0.wireOp",EDGE,"E82")}),1.0]])]});
            var Q5;
            Q5=makeQuery(id+"F0.imprint","IMPRINT",FACE,{"disambiguationData":[TD([[makeQuery(id+"F0.imprint","IMPRINT",EDGE,{"derivedFrom":sQuery(id+"F0.wireOp",EDGE,"E98")}),1.0]])]});
            var Q6;
            Q6=makeQuery(id+"F0.imprint","IMPRINT",FACE,{"disambiguationData":[TD([[makeQuery(id+"F0.imprint","IMPRINT",EDGE,{"derivedFrom":sQuery(id+"F0.wireOp",EDGE,"E76")}),1.0]])]});
            var Q7;
            Q7=makeQuery(id+"F0.imprint","IMPRINT",FACE,{"disambiguationData":[TD([[makeQuery(id+"F0.imprint","IMPRINT",EDGE,{"derivedFrom":sQuery(id+"F0.wireOp",EDGE,"E84")}),1.0]])]});
            var Q8;
            Q8=makeQuery(id+"F0.imprint","IMPRINT",FACE,{"disambiguationData":[TD([[makeQuery(id+"F0.imprint","IMPRINT",EDGE,{"derivedFrom":sQuery(id+"F0.wireOp",EDGE,"E139")}),1.0]])]});
            var Q9;
            Q9=makeQuery(id+"F0.imprint","IMPRINT",FACE,{"disambiguationData":[TD([[makeQuery(id+"F0.imprint","IMPRINT",EDGE,{"derivedFrom":sQuery(id+"F0.wireOp",EDGE,"E100")}),1.0]])]});
            var Q10;
            Q10=makeQuery(id+"F0.imprint","IMPRINT",FACE,{"disambiguationData":[TD([[makeQuery(id+"F0.imprint","IMPRINT",EDGE,{"derivedFrom":sQuery(id+"F0.wireOp",EDGE,"E35")}),1.0]])]});
            var Q11;
            Q11=makeQuery(id+"F0.imprint","IMPRINT",FACE,{"disambiguationData":[TD([[makeQuery(id+"F0.imprint","IMPRINT",EDGE,{"derivedFrom":sQuery(id+"F0.wireOp",EDGE,"E74")}),1.0]])]});
            var Q12;
            Q12=makeQuery(id+"F0.imprint","IMPRINT",FACE,{"disambiguationData":[TD([[makeQuery(id+"F0.imprint","IMPRINT",EDGE,{"derivedFrom":sQuery(id+"F0.wireOp",EDGE,"E146")}),1.0]])]});
            var Q13;
            Q13=makeQuery(id+"F0.imprint","IMPRINT",FACE,{"disambiguationData":[TD([[makeQuery(id+"F0.imprint","IMPRINT",EDGE,{"derivedFrom":sQuery(id+"F0.wireOp",EDGE,"E69")}),1.0]])]});
            var Q14;
            Q14=makeQuery(id+"F0.imprint","IMPRINT",FACE,{"disambiguationData":[TD([[makeQuery(id+"F0.imprint","IMPRINT",EDGE,{"derivedFrom":sQuery(id+"F0.wireOp",EDGE,"E130")}),1.0]])]});
            var Q15;
            Q15=makeQuery(id+"F0.imprint","IMPRINT",FACE,{"disambiguationData":[TD([[makeQuery(id+"F0.imprint","IMPRINT",EDGE,{"derivedFrom":sQuery(id+"F0.wireOp",EDGE,"E38")}),1.0]])]});
            var Q16;
            Q16=makeQuery(id+"F0.imprint","IMPRINT",FACE,{"disambiguationData":[TD([[makeQuery(id+"F0.imprint","IMPRINT",EDGE,{"derivedFrom":sQuery(id+"F0.wireOp",EDGE,"E129")}),1.0]])]});
            var Q17;
            Q17=makeQuery(id+"F0.imprint","IMPRINT",FACE,{"disambiguationData":[TD([[makeQuery(id+"F0.imprint","IMPRINT",EDGE,{"derivedFrom":sQuery(id+"F0.wireOp",EDGE,"E138")}),1.0]])]});
            var Q18;
            Q18=makeQuery(id+"F0.imprint","IMPRINT",FACE,{"disambiguationData":[TD([[makeQuery(id+"F0.imprint","IMPRINT",EDGE,{"derivedFrom":sQuery(id+"F0.wireOp",EDGE,"E68")}),1.0]])]});
            var Q19;
            Q19=makeQuery(id+"F0.imprint","IMPRINT",FACE,{"disambiguationData":[TD([[makeQuery(id+"F0.imprint","IMPRINT",EDGE,{"derivedFrom":sQuery(id+"F0.wireOp",EDGE,"E137")}),1.0]])]});
            var Q20;
            Q20=makeQuery(id+"F0.imprint","IMPRINT",FACE,{"disambiguationData":[TD([[makeQuery(id+"F0.imprint","IMPRINT",EDGE,{"derivedFrom":sQuery(id+"F0.wireOp",EDGE,"E99")}),1.0]])]});
            var Q21;
            Q21=makeQuery(id+"F0.imprint","IMPRINT",FACE,{"disambiguationData":[TD([[makeQuery(id+"F0.imprint","IMPRINT",EDGE,{"derivedFrom":sQuery(id+"F0.wireOp",EDGE,"E36")}),1.0]])]});
            var Q22;
            Q22=makeQuery(id+"F0.imprint","IMPRINT",FACE,{"disambiguationData":[TD([[makeQuery(id+"F0.imprint","IMPRINT",EDGE,{"derivedFrom":sQuery(id+"F0.wireOp",EDGE,"E145")}),1.0]])]});
            var Q23;
            Q23=makeQuery(id+"F0.imprint","IMPRINT",FACE,{"disambiguationData":[TD([[makeQuery(id+"F0.imprint","IMPRINT",EDGE,{"derivedFrom":sQuery(id+"F0.wireOp",EDGE,"E144")}),1.0]])]});
            var Q24;
            Q24=makeQuery(id+"F0.imprint","IMPRINT",FACE,{"disambiguationData":[TD([[makeQuery(id+"F0.imprint","IMPRINT",EDGE,{"derivedFrom":sQuery(id+"F0.wireOp",EDGE,"E75")}),1.0]])]});
            var Q25;
            Q25=makeQuery(id+"F0.imprint","IMPRINT",FACE,{"disambiguationData":[TD([[makeQuery(id+"F0.imprint","IMPRINT",EDGE,{"derivedFrom":sQuery(id+"F0.wireOp",EDGE,"E67")}),1.0]])]});
            var Q26;
            Q26=makeQuery(id+"F0.imprint","IMPRINT",FACE,{"disambiguationData":[TD([[makeQuery(id+"F0.imprint","IMPRINT",EDGE,{"derivedFrom":sQuery(id+"F0.wireOp",EDGE,"E83")}),1.0]])]});
            var Q27;
            Q27=makeQuery(id+"F0.imprint","IMPRINT",FACE,{"disambiguationData":[TD([[makeQuery(id+"F0.imprint","IMPRINT",EDGE,{"derivedFrom":sQuery(id+"F0.wireOp",EDGE,"E131")}),1.0]])]});
            var Q28;
            Q28=makeQuery(id+"F0.imprint","IMPRINT",FACE,{"disambiguationData":[TD([[makeQuery(id+"F0.imprint","IMPRINT",EDGE,{"derivedFrom":sQuery(id+"F0.wireOp",EDGE,"E37")}),1.0]])]});
            var Q29;
            Q29=makeQuery(id+"F0.imprint","IMPRINT",FACE,{"disambiguationData":[TD([[makeQuery(id+"F0.imprint","IMPRINT",EDGE,{"derivedFrom":sQuery(id+"F0.wireOp",EDGE,"E97")}),1.0]])]});
            var Q30;
            Q30=makeQuery(id+"F0.imprint","IMPRINT",FACE,{"disambiguationData":[TD([[makeQuery(id+"F0.imprint","IMPRINT",EDGE,{"derivedFrom":sQuery(id+"F0.wireOp",EDGE,"E147")}),1.0]])]});
            var Q31;
            Q31=makeQuery(id+"F0.imprint","IMPRINT",FACE,{"disambiguationData":[TD([[makeQuery(id+"F0.imprint","IMPRINT",EDGE,{"derivedFrom":sQuery(id+"F0.wireOp",EDGE,"E85")}),1.0]])]});
            extrude(context, id + "F13", {"entities" : qUnion([Q0, Q1, Q2, Q3, Q4, Q5, Q6, Q7, Q8, Q9, Q10, Q11, Q12, Q13, Q14, Q15, Q16, Q17, Q18, Q19, Q20, Q21, Q22, Q23, Q24, Q25, Q26, Q27, Q28, Q29, Q30, Q31]), "operationType" : NewBodyOperationType.ADD, "oppositeDirection" : true, "depth" : 1.59 * mm, "offsetDistance" : 25.4 * mm});
        }
        {
            var Q0;
            Q0=makeQuery(id+"F0.imprint","IMPRINT",FACE,{"disambiguationData":[TD([[makeQuery(id+"F0.imprint","IMPRINT",EDGE,{"derivedFrom":sQuery(id+"F0.wireOp",EDGE,"E122")}),1.0]])]});
            var Q1;
            Q1=makeQuery(id+"F0.imprint","IMPRINT",FACE,{"disambiguationData":[TD([[makeQuery(id+"F0.imprint","IMPRINT",EDGE,{"derivedFrom":sQuery(id+"F0.wireOp",EDGE,"E154")}),1.0]])]});
            var Q2;
            Q2=makeQuery(id+"F0.imprint","IMPRINT",FACE,{"disambiguationData":[TD([[makeQuery(id+"F0.imprint","IMPRINT",EDGE,{"derivedFrom":sQuery(id+"F0.wireOp",EDGE,"E92")}),1.0]])]});
            var Q3;
            Q3=makeQuery(id+"F0.imprint","IMPRINT",FACE,{"disambiguationData":[TD([[makeQuery(id+"F0.imprint","IMPRINT",EDGE,{"derivedFrom":sQuery(id+"F0.wireOp",EDGE,"E91")}),1.0]])]});
            var Q4;
            Q4=makeQuery(id+"F0.imprint","IMPRINT",FACE,{"disambiguationData":[TD([[makeQuery(id+"F0.imprint","IMPRINT",EDGE,{"derivedFrom":sQuery(id+"F0.wireOp",EDGE,"E153")}),1.0]])]});
            var Q5;
            Q5=makeQuery(id+"F0.imprint","IMPRINT",FACE,{"disambiguationData":[TD([[makeQuery(id+"F0.imprint","IMPRINT",EDGE,{"derivedFrom":sQuery(id+"F0.wireOp",EDGE,"E123")}),1.0]])]});
            extrude(context, id + "F14", {"entities" : qUnion([Q0, Q1, Q2, Q3, Q4, Q5]), "operationType" : NewBodyOperationType.ADD, "oppositeDirection" : true, "depth" : 1.59 * mm, "offsetDistance" : 25.4 * mm});
        }
        {
            var Q0;
            Q0=makeQuery(id+"F0.imprint","IMPRINT",FACE,{"disambiguationData":[TD([[makeQuery(id+"F0.imprint","IMPRINT",EDGE,{"derivedFrom":sQuery(id+"F0.wireOp",EDGE,"E60")}),1.0]])]});
            var Q1;
            Q1=makeQuery(id+"F0.imprint","IMPRINT",FACE,{"disambiguationData":[TD([[makeQuery(id+"F0.imprint","IMPRINT",EDGE,{"derivedFrom":sQuery(id+"F0.wireOp",EDGE,"E61")}),1.0]])]});
            extrude(context, id + "F15", {"entities" : qUnion([Q0, Q1]), "operationType" : NewBodyOperationType.ADD, "oppositeDirection" : true, "depth" : 1.59 * mm, "offsetDistance" : 25.4 * mm});
        }
        {
            var Q0;
            Q0=makeQuery(id+"F12.opExtrude","CAP_FACE",FACE,{"disambiguationData":[OSD([sQuery(id+"F0.wireOp",EDGE,"E55.bottom"),sQuery(id+"F0.wireOp",EDGE,"E55.top"),sQuery(id+"F0.wireOp",EDGE,"E55.left"),sQuery(id+"F0.wireOp",EDGE,"E55.right")])],"isStart":false});
            var Q1;
            Q1=makeQuery(id+"F7.opExtrude","CAP_FACE",FACE,{"disambiguationData":[OSD([sQuery(id+"F0.wireOp",EDGE,"E24.bottom"),sQuery(id+"F0.wireOp",EDGE,"E24.top"),sQuery(id+"F0.wireOp",EDGE,"E24.left"),sQuery(id+"F0.wireOp",EDGE,"E24.right")])],"isStart":false});
            var Q2;
            Q2=makeQuery(id+"F7.opExtrude","CAP_FACE",FACE,{"disambiguationData":[OSD([sQuery(id+"F0.wireOp",EDGE,"E39.bottom"),sQuery(id+"F0.wireOp",EDGE,"E39.top"),sQuery(id+"F0.wireOp",EDGE,"E39.right"),sQuery(id+"F0.wireOp",EDGE,"E47.bottom"),sQuery(id+"F0.wireOp",EDGE,"E47.top"),sQuery(id+"F0.wireOp",EDGE,"E155.bottom"),sQuery(id+"F0.wireOp",EDGE,"E155.top"),sQuery(id+"F0.wireOp",EDGE,"E155.right")])],"isStart":false});
            var Q3;
            Q3=makeQuery(id+"F12.opExtrude","CAP_FACE",FACE,{"disambiguationData":[OSD([sQuery(id+"F0.wireOp",EDGE,"E31.top"),sQuery(id+"F0.wireOp",EDGE,"E31.right"),sQuery(id+"F0.wireOp",EDGE,"E62.top"),sQuery(id+"F0.wireOp",EDGE,"E70.top"),sQuery(id+"F0.wireOp",EDGE,"E78.top"),sQuery(id+"F0.wireOp",EDGE,"E78.left"),sQuery(id+"F0.wireOp",EDGE,"E93.bottom"),sQuery(id+"F0.wireOp",EDGE,"E93.right"),sQuery(id+"F0.wireOp",EDGE,"E124.bottom"),sQuery(id+"F0.wireOp",EDGE,"E132.bottom"),sQuery(id+"F0.wireOp",EDGE,"E140.bottom"),sQuery(id+"F0.wireOp",EDGE,"E140.left")])],"isStart":false});
            var Q4;
            Q4=makeQuery(id+"F8.opExtrude","CAP_FACE",FACE,{"disambiguationData":[OSD([sQuery(id+"F0.wireOp",EDGE,"E101.bottom"),sQuery(id+"F0.wireOp",EDGE,"E101.top"),sQuery(id+"F0.wireOp",EDGE,"E101.right"),sQuery(id+"F0.wireOp",EDGE,"E109.bottom"),sQuery(id+"F0.wireOp",EDGE,"E109.top"),sQuery(id+"F0.wireOp",EDGE,"E109.left")])],"isStart":false});
            var Q5;
            Q5=makeQuery(id+"F12.opExtrude","CAP_FACE",FACE,{"disambiguationData":[OSD([sQuery(id+"F0.wireOp",EDGE,"E86.top"),sQuery(id+"F0.wireOp",EDGE,"E86.left"),sQuery(id+"F0.wireOp",EDGE,"E86.right"),sQuery(id+"F0.wireOp",EDGE,"E117.bottom"),sQuery(id+"F0.wireOp",EDGE,"E117.left"),sQuery(id+"F0.wireOp",EDGE,"E117.right"),sQuery(id+"F0.wireOp",EDGE,"E148.left"),sQuery(id+"F0.wireOp",EDGE,"E148.right")])],"isStart":false});
            shell(context, id + "F16", {"entities" : qUnion([Q0, Q1, Q2, Q3, Q4, Q5]), "thickness" : 1.59 * mm});
        }
        {
            var Q0;
            Q0=makeQuery(id+"F0.imprint","IMPRINT",FACE,{"disambiguationData":[TD([[makeQuery(id+"F0.imprint","IMPRINT",EDGE,{"derivedFrom":sQuery(id+"F0.wireOp",EDGE,"E231")}),1.0]])]});
            var Q1;
            Q1=makeQuery(id+"F0.imprint","IMPRINT",FACE,{"disambiguationData":[TD([[makeQuery(id+"F0.imprint","IMPRINT",EDGE,{"derivedFrom":sQuery(id+"F0.wireOp",EDGE,"E225.bottom")}),-1.0]])]});
            var Q2;
            Q2=makeQuery(id+"F0.imprint","IMPRINT",FACE,{"disambiguationData":[TD([[makeQuery(id+"F0.imprint","IMPRINT",EDGE,{"derivedFrom":sQuery(id+"F0.wireOp",EDGE,"E199")}),1.0]])]});
            var Q3;
            Q3=makeQuery(id+"F0.imprint","IMPRINT",FACE,{"disambiguationData":[TD([[makeQuery(id+"F0.imprint","IMPRINT",EDGE,{"derivedFrom":sQuery(id+"F0.wireOp",EDGE,"E194.top")}),1.0]])]});
            var Q4;
            Q4=makeQuery(id+"F0.imprint","IMPRINT",FACE,{"disambiguationData":[TD([[makeQuery(id+"F0.imprint","IMPRINT",EDGE,{"derivedFrom":sQuery(id+"F0.wireOp",EDGE,"E230")}),1.0]])]});
            var Q5;
            Q5=makeQuery(id+"F0.imprint","IMPRINT",FACE,{"disambiguationData":[TD([[makeQuery(id+"F0.imprint","IMPRINT",EDGE,{"derivedFrom":sQuery(id+"F0.wireOp",EDGE,"E200")}),1.0]])]});
            var Q6;
            Q6=makeQuery(id+"F0.imprint","IMPRINT",FACE,{"disambiguationData":[TD([[makeQuery(id+"F0.imprint","IMPRINT",EDGE,{"derivedFrom":sQuery(id+"F0.wireOp",EDGE,"E186.bottom")}),-1.0]])]});
            var Q7;
            Q7=makeQuery(id+"F0.imprint","IMPRINT",FACE,{"disambiguationData":[TD([[makeQuery(id+"F0.imprint","IMPRINT",EDGE,{"derivedFrom":sQuery(id+"F0.wireOp",EDGE,"E178.bottom")}),-1.0]])]});
            var Q8;
            Q8=makeQuery(id+"F0.imprint","IMPRINT",FACE,{"disambiguationData":[TD([[makeQuery(id+"F0.imprint","IMPRINT",EDGE,{"derivedFrom":sQuery(id+"F0.wireOp",EDGE,"E190")}),1.0]])]});
            var Q9;
            Q9=makeQuery(id+"F0.imprint","IMPRINT",FACE,{"disambiguationData":[TD([[makeQuery(id+"F0.imprint","IMPRINT",EDGE,{"derivedFrom":sQuery(id+"F0.wireOp",EDGE,"E191")}),1.0]])]});
            var Q10;
            Q10=makeQuery(id+"F0.imprint","IMPRINT",FACE,{"disambiguationData":[TD([[makeQuery(id+"F0.imprint","IMPRINT",EDGE,{"derivedFrom":sQuery(id+"F0.wireOp",EDGE,"E193")}),1.0]])]});
            var Q11;
            Q11=makeQuery(id+"F0.imprint","IMPRINT",FACE,{"disambiguationData":[TD([[makeQuery(id+"F0.imprint","IMPRINT",EDGE,{"derivedFrom":sQuery(id+"F0.wireOp",EDGE,"E192")}),1.0]])]});
            var Q12;
            Q12=makeQuery(id+"F0.imprint","IMPRINT",FACE,{"disambiguationData":[TD([[makeQuery(id+"F0.imprint","IMPRINT",EDGE,{"derivedFrom":sQuery(id+"F0.wireOp",EDGE,"E184")}),1.0]])]});
            var Q13;
            Q13=makeQuery(id+"F0.imprint","IMPRINT",FACE,{"disambiguationData":[TD([[makeQuery(id+"F0.imprint","IMPRINT",EDGE,{"derivedFrom":sQuery(id+"F0.wireOp",EDGE,"E183")}),1.0]])]});
            var Q14;
            Q14=makeQuery(id+"F0.imprint","IMPRINT",FACE,{"disambiguationData":[TD([[makeQuery(id+"F0.imprint","IMPRINT",EDGE,{"derivedFrom":sQuery(id+"F0.wireOp",EDGE,"E182")}),1.0]])]});
            var Q15;
            Q15=makeQuery(id+"F0.imprint","IMPRINT",FACE,{"disambiguationData":[TD([[makeQuery(id+"F0.imprint","IMPRINT",EDGE,{"derivedFrom":sQuery(id+"F0.wireOp",EDGE,"E185")}),1.0]])]});
            var Q16;
            Q16=makeQuery(id+"F0.imprint","IMPRINT",FACE,{"disambiguationData":[TD([[makeQuery(id+"F0.imprint","IMPRINT",EDGE,{"derivedFrom":sQuery(id+"F0.wireOp",EDGE,"E217.bottom")}),-1.0]])]});
            var Q17;
            Q17=makeQuery(id+"F0.imprint","IMPRINT",FACE,{"disambiguationData":[TD([[makeQuery(id+"F0.imprint","IMPRINT",EDGE,{"derivedFrom":sQuery(id+"F0.wireOp",EDGE,"E222")}),1.0]])]});
            var Q18;
            Q18=makeQuery(id+"F0.imprint","IMPRINT",FACE,{"disambiguationData":[TD([[makeQuery(id+"F0.imprint","IMPRINT",EDGE,{"derivedFrom":sQuery(id+"F0.wireOp",EDGE,"E221")}),1.0]])]});
            var Q19;
            Q19=makeQuery(id+"F0.imprint","IMPRINT",FACE,{"disambiguationData":[TD([[makeQuery(id+"F0.imprint","IMPRINT",EDGE,{"derivedFrom":sQuery(id+"F0.wireOp",EDGE,"E224")}),1.0]])]});
            var Q20;
            Q20=makeQuery(id+"F0.imprint","IMPRINT",FACE,{"disambiguationData":[TD([[makeQuery(id+"F0.imprint","IMPRINT",EDGE,{"derivedFrom":sQuery(id+"F0.wireOp",EDGE,"E223")}),1.0]])]});
            var Q21;
            Q21=makeQuery(id+"F0.imprint","IMPRINT",FACE,{"disambiguationData":[TD([[makeQuery(id+"F0.imprint","IMPRINT",EDGE,{"derivedFrom":sQuery(id+"F0.wireOp",EDGE,"E214")}),1.0]])]});
            var Q22;
            Q22=makeQuery(id+"F0.imprint","IMPRINT",FACE,{"disambiguationData":[TD([[makeQuery(id+"F0.imprint","IMPRINT",EDGE,{"derivedFrom":sQuery(id+"F0.wireOp",EDGE,"E213")}),1.0]])]});
            var Q23;
            Q23=makeQuery(id+"F0.imprint","IMPRINT",FACE,{"disambiguationData":[TD([[makeQuery(id+"F0.imprint","IMPRINT",EDGE,{"derivedFrom":sQuery(id+"F0.wireOp",EDGE,"E209.bottom")}),-1.0]])]});
            var Q24;
            Q24=makeQuery(id+"F0.imprint","IMPRINT",FACE,{"disambiguationData":[TD([[makeQuery(id+"F0.imprint","IMPRINT",EDGE,{"derivedFrom":sQuery(id+"F0.wireOp",EDGE,"E216")}),1.0]])]});
            var Q25;
            Q25=makeQuery(id+"F0.imprint","IMPRINT",FACE,{"disambiguationData":[TD([[makeQuery(id+"F0.imprint","IMPRINT",EDGE,{"derivedFrom":sQuery(id+"F0.wireOp",EDGE,"E215")}),1.0]])]});
            extrude(context, id + "F17", {"entities" : qUnion([Q0, Q1, Q2, Q3, Q4, Q5, Q6, Q7, Q8, Q9, Q10, Q11, Q12, Q13, Q14, Q15, Q16, Q17, Q18, Q19, Q20, Q21, Q22, Q23, Q24, Q25]), "depth" : 3.17 * mm, "offsetDistance" : 25.4 * mm});
        }
        {
            var Q0;
            Q0=makeQuery(id+"F0.imprint","IMPRINT",FACE,{"disambiguationData":[TD([[makeQuery(id+"F0.imprint","IMPRINT",EDGE,{"derivedFrom":sQuery(id+"F0.wireOp",EDGE,"E213")}),1.0]])]});
            var Q1;
            Q1=makeQuery(id+"F0.imprint","IMPRINT",FACE,{"disambiguationData":[TD([[makeQuery(id+"F0.imprint","IMPRINT",EDGE,{"derivedFrom":sQuery(id+"F0.wireOp",EDGE,"E222")}),1.0]])]});
            var Q2;
            Q2=makeQuery(id+"F0.imprint","IMPRINT",FACE,{"disambiguationData":[TD([[makeQuery(id+"F0.imprint","IMPRINT",EDGE,{"derivedFrom":sQuery(id+"F0.wireOp",EDGE,"E184")}),1.0]])]});
            var Q3;
            Q3=makeQuery(id+"F0.imprint","IMPRINT",FACE,{"disambiguationData":[TD([[makeQuery(id+"F0.imprint","IMPRINT",EDGE,{"derivedFrom":sQuery(id+"F0.wireOp",EDGE,"E192")}),1.0]])]});
            var Q4;
            Q4=makeQuery(id+"F0.imprint","IMPRINT",FACE,{"disambiguationData":[TD([[makeQuery(id+"F0.imprint","IMPRINT",EDGE,{"derivedFrom":sQuery(id+"F0.wireOp",EDGE,"E223")}),1.0]])]});
            var Q5;
            Q5=makeQuery(id+"F0.imprint","IMPRINT",FACE,{"disambiguationData":[TD([[makeQuery(id+"F0.imprint","IMPRINT",EDGE,{"derivedFrom":sQuery(id+"F0.wireOp",EDGE,"E191")}),1.0]])]});
            var Q6;
            Q6=makeQuery(id+"F0.imprint","IMPRINT",FACE,{"disambiguationData":[TD([[makeQuery(id+"F0.imprint","IMPRINT",EDGE,{"derivedFrom":sQuery(id+"F0.wireOp",EDGE,"E224")}),1.0]])]});
            var Q7;
            Q7=makeQuery(id+"F0.imprint","IMPRINT",FACE,{"disambiguationData":[TD([[makeQuery(id+"F0.imprint","IMPRINT",EDGE,{"derivedFrom":sQuery(id+"F0.wireOp",EDGE,"E216")}),1.0]])]});
            var Q8;
            Q8=makeQuery(id+"F0.imprint","IMPRINT",FACE,{"disambiguationData":[TD([[makeQuery(id+"F0.imprint","IMPRINT",EDGE,{"derivedFrom":sQuery(id+"F0.wireOp",EDGE,"E221")}),1.0]])]});
            var Q9;
            Q9=makeQuery(id+"F0.imprint","IMPRINT",FACE,{"disambiguationData":[TD([[makeQuery(id+"F0.imprint","IMPRINT",EDGE,{"derivedFrom":sQuery(id+"F0.wireOp",EDGE,"E193")}),1.0]])]});
            var Q10;
            Q10=makeQuery(id+"F0.imprint","IMPRINT",FACE,{"disambiguationData":[TD([[makeQuery(id+"F0.imprint","IMPRINT",EDGE,{"derivedFrom":sQuery(id+"F0.wireOp",EDGE,"E183")}),1.0]])]});
            var Q11;
            Q11=makeQuery(id+"F0.imprint","IMPRINT",FACE,{"disambiguationData":[TD([[makeQuery(id+"F0.imprint","IMPRINT",EDGE,{"derivedFrom":sQuery(id+"F0.wireOp",EDGE,"E215")}),1.0]])]});
            var Q12;
            Q12=makeQuery(id+"F0.imprint","IMPRINT",FACE,{"disambiguationData":[TD([[makeQuery(id+"F0.imprint","IMPRINT",EDGE,{"derivedFrom":sQuery(id+"F0.wireOp",EDGE,"E182")}),1.0]])]});
            var Q13;
            Q13=makeQuery(id+"F0.imprint","IMPRINT",FACE,{"disambiguationData":[TD([[makeQuery(id+"F0.imprint","IMPRINT",EDGE,{"derivedFrom":sQuery(id+"F0.wireOp",EDGE,"E185")}),1.0]])]});
            var Q14;
            Q14=makeQuery(id+"F0.imprint","IMPRINT",FACE,{"disambiguationData":[TD([[makeQuery(id+"F0.imprint","IMPRINT",EDGE,{"derivedFrom":sQuery(id+"F0.wireOp",EDGE,"E214")}),1.0]])]});
            var Q15;
            Q15=makeQuery(id+"F0.imprint","IMPRINT",FACE,{"disambiguationData":[TD([[makeQuery(id+"F0.imprint","IMPRINT",EDGE,{"derivedFrom":sQuery(id+"F0.wireOp",EDGE,"E190")}),1.0]])]});
            extrude(context, id + "F18", {"entities" : qUnion([Q0, Q1, Q2, Q3, Q4, Q5, Q6, Q7, Q8, Q9, Q10, Q11, Q12, Q13, Q14, Q15]), "operationType" : NewBodyOperationType.ADD, "oppositeDirection" : true, "depth" : 1.59 * mm, "offsetDistance" : 25.4 * mm});
        }
        {
            var Q0;
            Q0=makeQuery(id+"F0.imprint","IMPRINT",FACE,{"disambiguationData":[TD([[makeQuery(id+"F0.imprint","IMPRINT",EDGE,{"derivedFrom":sQuery(id+"F0.wireOp",EDGE,"E231")}),1.0]])]});
            var Q1;
            Q1=makeQuery(id+"F0.imprint","IMPRINT",FACE,{"disambiguationData":[TD([[makeQuery(id+"F0.imprint","IMPRINT",EDGE,{"derivedFrom":sQuery(id+"F0.wireOp",EDGE,"E230")}),1.0]])]});
            var Q2;
            Q2=makeQuery(id+"F0.imprint","IMPRINT",FACE,{"disambiguationData":[TD([[makeQuery(id+"F0.imprint","IMPRINT",EDGE,{"derivedFrom":sQuery(id+"F0.wireOp",EDGE,"E199")}),1.0]])]});
            var Q3;
            Q3=makeQuery(id+"F0.imprint","IMPRINT",FACE,{"disambiguationData":[TD([[makeQuery(id+"F0.imprint","IMPRINT",EDGE,{"derivedFrom":sQuery(id+"F0.wireOp",EDGE,"E200")}),1.0]])]});
            extrude(context, id + "F19", {"entities" : qUnion([Q0, Q1, Q2, Q3]), "operationType" : NewBodyOperationType.ADD, "oppositeDirection" : true, "depth" : 1.59 * mm, "offsetDistance" : 25.4 * mm});
        }
        {
            var Q0;
            Q0=makeQuery(id+"F17.opExtrude","CAP_FACE",FACE,{"disambiguationData":[OSD([sQuery(id+"F0.wireOp",EDGE,"E194.top"),sQuery(id+"F0.wireOp",EDGE,"E194.left"),sQuery(id+"F0.wireOp",EDGE,"E194.right"),sQuery(id+"F0.wireOp",EDGE,"E225.bottom"),sQuery(id+"F0.wireOp",EDGE,"E225.left"),sQuery(id+"F0.wireOp",EDGE,"E225.right")])],"isStart":false});
            var Q1;
            Q1=makeQuery(id+"F17.opExtrude","CAP_FACE",FACE,{"disambiguationData":[OSD([sQuery(id+"F0.wireOp",EDGE,"E178.bottom"),sQuery(id+"F0.wireOp",EDGE,"E178.top"),sQuery(id+"F0.wireOp",EDGE,"E186.bottom"),sQuery(id+"F0.wireOp",EDGE,"E186.top"),sQuery(id+"F0.wireOp",EDGE,"E186.left"),sQuery(id+"F0.wireOp",EDGE,"E209.bottom"),sQuery(id+"F0.wireOp",EDGE,"E209.top"),sQuery(id+"F0.wireOp",EDGE,"E209.right"),sQuery(id+"F0.wireOp",EDGE,"E217.bottom"),sQuery(id+"F0.wireOp",EDGE,"E217.top")])],"isStart":false});
            shell(context, id + "F20", {"entities" : qUnion([Q0, Q1]), "thickness" : 1.59 * mm});
        }
    });
